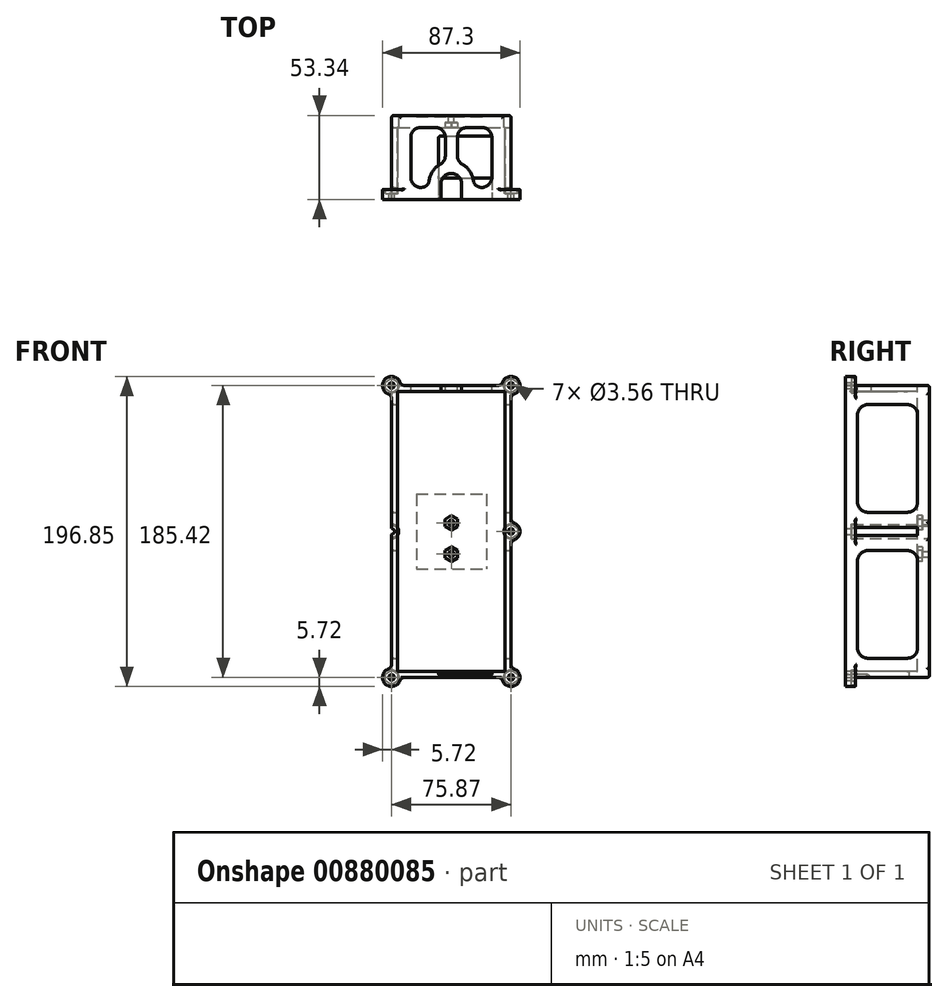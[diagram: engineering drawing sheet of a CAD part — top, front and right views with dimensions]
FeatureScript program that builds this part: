
annotation { "Feature Type Name" : "Feature", "Feature Type Description" : "" }
export const myFeature = defineFeature(function(context is Context, id is Id, definition is map)
    precondition{}
    {
        {
            var Q0;
            Q0=qCreatedBy(makeId("Front.planeOp"),FACE);
            var sketch = newSketch(context, id + "F0", { "sketchPlane" : qUnion([Q0])});
            skLineSegment(sketch, "E0.bottom", {"start": v(0, 0) * mm, "end": v(75.87, 0) * mm});
            skLineSegment(sketch, "E0.top", {"start": v(0, 185.42) * mm, "end": v(75.87, 185.42) * mm});
            skLineSegment(sketch, "E0.left", {"start": v(0, 0) * mm, "end": v(0, 185.42) * mm});
            skLineSegment(sketch, "E0.right", {"start": v(75.87, 0) * mm, "end": v(75.87, 185.42) * mm});
            skSolve(sketch);
        }
        {
            var Q0;
            Q0=makeQuery(id+"F0.imprint","IMPRINT",FACE,{"disambiguationData":[TD([[makeQuery(id+"F0.imprint","IMPRINT",EDGE,{"derivedFrom":sQuery(id+"F0.wireOp",EDGE,"E0.bottom")}),1.0]])]});
            extrude(context, id + "F1", {"entities" : qUnion([Q0]), "oppositeDirection" : true, "depth" : 53.34 * mm, "offsetDistance" : 25.4 * mm});
        }
        {
            var Q0;
            Q0=makeQuery(id+"F1.opExtrude","CAP_FACE",FACE,{"disambiguationData":[OSD([sQuery(id+"F0.wireOp",EDGE,"E0.bottom"),sQuery(id+"F0.wireOp",EDGE,"E0.top"),sQuery(id+"F0.wireOp",EDGE,"E0.left"),sQuery(id+"F0.wireOp",EDGE,"E0.right")])],"isStart":true});
            var sketch = newSketch(context, id + "F2", { "sketchPlane" : qUnion([Q0])});
            skLineSegment(sketch, "E1.0", {"start": v(72.06, 3.8) * mm, "end": v(72.06, 181.6) * mm});
            skLineSegment(sketch, "E2.0", {"start": v(3.81, 3.8) * mm, "end": v(3.8, 181.6) * mm});
            skLineSegment(sketch, "E3.0", {"start": v(3.81, 3.8) * mm, "end": v(72.06, 3.8) * mm});
            skLineSegment(sketch, "E4.0", {"start": v(3.8, 181.6) * mm, "end": v(72.06, 181.6) * mm});
            skSolve(sketch);
        }
        {
            var Q0;
            Q0=makeQuery(id+"F2.imprint","IMPRINT",FACE,{"disambiguationData":[TD([[makeQuery(id+"F2.imprint","IMPRINT",EDGE,{"derivedFrom":sQuery(id+"F2.wireOp",EDGE,"E1.0")}),1.0]])]});
            extrude(context, id + "F3", {"entities" : qUnion([Q0]), "operationType" : NewBodyOperationType.REMOVE, "oppositeDirection" : true, "depth" : 45.72 * mm, "offsetDistance" : 25.4 * mm});
        }
        {
            var Q0;
            Q0=makeQuery(id+"F1.opExtrude","SWEPT_FACE",FACE,{"disambiguationData":[OSD([sQuery(id+"F0.wireOp",EDGE,"E0.top")])]});
            var sketch = newSketch(context, id + "F4", { "sketchPlane" : qUnion([Q0])});
            skLineSegment(sketch, "E5.0", {"start": v(44.48, 0) * mm, "end": v(44.48, 9.98) * mm});
            skLineSegment(sketch, "E6.0", {"start": v(31.4, 0) * mm, "end": v(31.4, 9.98) * mm});
            skLineSegment(sketch, "E7.0", {"start": v(37.92, 16.51) * mm, "end": v(37.95, 16.51) * mm});
            skPoint(sketch, "E8.orphan", {"position": v(37.93, 53.34) * mm});
            skPoint(sketch, "E9.start.orphan", {"position": v(37.93, 0) * mm});
            skPoint(sketch, "E10.visualSharp", {"position": v(31.4, 16.51) * mm});
            skArc(sketch, "E10.filletArc", {"start": v(31.78, 16.51) * mm, "mid": v(31.5, 16.4) * mm, "end": v(31.4, 16.13) * mm});
            skArc(sketch, "E11.filletArc", {"start": v(37.92, 16.51) * mm, "mid": v(33.3, 14.6) * mm, "end": v(31.4, 9.98) * mm});
            skPoint(sketch, "E12.visualSharp", {"position": v(44.48, 16.51) * mm});
            skArc(sketch, "E12.filletArc", {"start": v(44.48, 9.98) * mm, "mid": v(42.56, 14.6) * mm, "end": v(37.95, 16.51) * mm});
            skLineSegment(sketch, "E13", {"start": v(44.48, 0) * mm, "end": v(31.4, 0) * mm});
            skSolve(sketch);
        }
        {
            var Q0;
            Q0=makeQuery(id+"F4.imprint","IMPRINT",FACE,{"disambiguationData":[TD([[makeQuery(id+"F4.imprint","IMPRINT",EDGE,{"derivedFrom":sQuery(id+"F4.wireOp",EDGE,"E5.0")}),1.0]])]});
            extrude(context, id + "F5", {"entities" : qUnion([Q0]), "operationType" : NewBodyOperationType.REMOVE, "oppositeDirection" : true, "depth" : 5.08 * mm, "offsetDistance" : 25.4 * mm});
        }
        {
            var Q0;
            Q0=makeQuery(id+"F1.opExtrude","SWEPT_FACE",FACE,{"disambiguationData":[OSD([sQuery(id+"F0.wireOp",EDGE,"E0.bottom")])]});
            var sketch = newSketch(context, id + "F6", { "sketchPlane" : qUnion([Q0])});
            skPoint(sketch, "E14.0", {"position": v(0, -53.34) * mm});
            skLineSegment(sketch, "E15.0", {"start": v(29.72, -38.86) * mm, "end": v(29.72, -14.73) * mm});
            skLineSegment(sketch, "E16.0", {"start": v(30.99, -40.13) * mm, "end": v(62.66, -40.13) * mm});
            skLineSegment(sketch, "E17.0", {"start": v(63.93, -38.86) * mm, "end": v(63.93, -14.73) * mm});
            skLineSegment(sketch, "E18.0", {"start": v(30.99, -13.46) * mm, "end": v(62.66, -13.46) * mm});
            skPoint(sketch, "E19.visualSharp", {"position": v(29.72, -13.46) * mm});
            skArc(sketch, "E19.filletArc", {"start": v(30.99, -13.46) * mm, "mid": v(30.09, -13.83) * mm, "end": v(29.72, -14.73) * mm});
            skPoint(sketch, "E20.visualSharp", {"position": v(29.72, -40.13) * mm});
            skArc(sketch, "E20.filletArc", {"start": v(29.72, -38.86) * mm, "mid": v(30.09, -39.76) * mm, "end": v(30.99, -40.13) * mm});
            skPoint(sketch, "E21.visualSharp", {"position": v(63.93, -13.46) * mm});
            skArc(sketch, "E21.filletArc", {"start": v(63.93, -14.73) * mm, "mid": v(63.56, -13.83) * mm, "end": v(62.66, -13.46) * mm});
            skPoint(sketch, "E22.visualSharp", {"position": v(63.93, -40.13) * mm});
            skArc(sketch, "E22.filletArc", {"start": v(62.66, -40.13) * mm, "mid": v(63.56, -39.76) * mm, "end": v(63.93, -38.86) * mm});
            skSolve(sketch);
        }
        {
            var Q0;
            Q0=makeQuery(id+"F6.imprint","IMPRINT",FACE,{"disambiguationData":[TD([[makeQuery(id+"F6.imprint","IMPRINT",EDGE,{"derivedFrom":sQuery(id+"F6.wireOp",EDGE,"E15.0")}),-1.0]])]});
            extrude(context, id + "F7", {"entities" : qUnion([Q0]), "operationType" : NewBodyOperationType.REMOVE, "oppositeDirection" : true, "depth" : 5.08 * mm, "offsetDistance" : 25.4 * mm});
        }
        {
            var Q0;
            Q0=makeQuery(id+"F1.opExtrude","CAP_FACE",FACE,{"disambiguationData":[OSD([sQuery(id+"F0.wireOp",EDGE,"E0.bottom"),sQuery(id+"F0.wireOp",EDGE,"E0.top"),sQuery(id+"F0.wireOp",EDGE,"E0.left"),sQuery(id+"F0.wireOp",EDGE,"E0.right")])],"isStart":true});
            var sketch = newSketch(context, id + "F8", { "sketchPlane" : qUnion([Q0])});
            skArc(sketch, "E23", {"start": v(4.57, 182) * mm, "mid": v(-4.04, 189.46) * mm, "end": v(3.43, 180.85) * mm});
            skArc(sketch, "E24", {"start": v(72.44, 180.85) * mm, "mid": v(79.91, 189.46) * mm, "end": v(71.3, 182) * mm});
            skArc(sketch, "E25", {"start": v(3.43, 4.57) * mm, "mid": v(-4.04, -4.04) * mm, "end": v(4.57, 3.43) * mm});
            skArc(sketch, "E26", {"start": v(71.3, 3.43) * mm, "mid": v(79.91, -4.04) * mm, "end": v(72.44, 4.57) * mm});
            skArc(sketch, "E27", {"start": v(72.44, 88.14) * mm, "mid": v(81.58, 92.71) * mm, "end": v(72.44, 97.28) * mm});
            skArc(sketch, "E28", {"start": v(3.43, 97.28) * mm, "mid": v(-5.71, 92.71) * mm, "end": v(3.43, 88.14) * mm});
            skLineSegment(sketch, "E29.0", {"start": v(3.43, 3.43) * mm, "end": v(3.43, 4.57) * mm});
            skLineSegment(sketch, "E30.trimOffspring", {"start": v(3.43, 180.85) * mm, "end": v(3.43, 182) * mm});
            skLineSegment(sketch, "E31.trimOffspring", {"start": v(3.43, 88.14) * mm, "end": v(3.43, 97.28) * mm});
            skLineSegment(sketch, "E32.0", {"start": v(72.44, 3.43) * mm, "end": v(72.44, 4.57) * mm});
            skLineSegment(sketch, "E33.trimOffspring", {"start": v(72.44, 180.85) * mm, "end": v(72.44, 182) * mm});
            skLineSegment(sketch, "E34.trimOffspring", {"start": v(72.44, 88.14) * mm, "end": v(72.44, 97.28) * mm});
            skLineSegment(sketch, "E35.0", {"start": v(71.3, 182) * mm, "end": v(72.44, 182) * mm});
            skLineSegment(sketch, "E36.0", {"start": v(3.43, 182) * mm, "end": v(4.57, 182) * mm});
            skLineSegment(sketch, "E37.0", {"start": v(3.43, 3.43) * mm, "end": v(4.57, 3.43) * mm});
            skLineSegment(sketch, "E38.trimOffspring", {"start": v(71.3, 3.43) * mm, "end": v(72.44, 3.43) * mm});
            skSolve(sketch);
        }
        {
            var Q0;
            {var subQ0=sQuery(id+"F8.wireOp",EDGE,"E24");var subQ1=sQuery(id+"F0.wireOp",EDGE,"E0.right");var subQ2=makeQuery(id+"F1.opExtrude","CAP_EDGE",EDGE,{"disambiguationData":[OSD([subQ1])],"isStart":true});var subQ3=makeQuery(id+"F8.imprint","INTERSECT",VERTEX,{"derivedFrom":[subQ2,subQ0]});Q0=makeQuery(id+"F8.imprint","IMPRINT",FACE,{"disambiguationData":[TD([[makeQuery(id+"F8.imprint","IMPRINT",EDGE,{"disambiguationData":[TD([[subQ3,-1.0]])],"derivedFrom":subQ0}),1.0]])]});}
            var Q1;
            {var subQ0=sQuery(id+"F8.wireOp",EDGE,"E23");var subQ1=sQuery(id+"F0.wireOp",EDGE,"E0.left");var subQ5=makeQuery(id+"F1.opExtrude","CAP_EDGE",EDGE,{"disambiguationData":[OSD([subQ1])],"isStart":true});var subQ6=makeQuery(id+"F8.imprint","INTERSECT",VERTEX,{"derivedFrom":[subQ5,subQ0]});Q1=makeQuery(id+"F8.imprint","IMPRINT",FACE,{"disambiguationData":[TD([[makeQuery(id+"F8.imprint","IMPRINT",EDGE,{"disambiguationData":[TD([[subQ6,1.0]])],"derivedFrom":subQ0}),1.0]])]});}
            var Q2;
            {var subQ0=sQuery(id+"F8.wireOp",EDGE,"E28");var subQ1=makeQuery(id+"F1.opExtrude","CAP_EDGE",EDGE,{"disambiguationData":[OSD([sQuery(id+"F0.wireOp",EDGE,"E0.left")])],"isStart":true});var subQ2=makeQuery(id+"F8.imprint","INTERSECT",VERTEX,{"disambiguationData":[OD(0.0)],"derivedFrom":[subQ1,subQ0]});Q2=makeQuery(id+"F8.imprint","IMPRINT",FACE,{"disambiguationData":[TD([[makeQuery(id+"F8.imprint","IMPRINT",EDGE,{"disambiguationData":[TD([[subQ2,-1.0]])],"derivedFrom":subQ0}),1.0]])]});}
            var Q3;
            {var subQ0=sQuery(id+"F8.wireOp",EDGE,"E31.trimOffspring");Q3=makeQuery(id+"F8.imprint","IMPRINT",FACE,{"disambiguationData":[TD([[makeQuery(id+"F8.imprint","IMPRINT",EDGE,{"derivedFrom":subQ0}),1.0]])]});}
            var Q4;
            {var subQ0=sQuery(id+"F8.wireOp",EDGE,"E27");var subQ1=makeQuery(id+"F1.opExtrude","CAP_EDGE",EDGE,{"disambiguationData":[OSD([sQuery(id+"F0.wireOp",EDGE,"E0.right")])],"isStart":true});var subQ2=makeQuery(id+"F8.imprint","INTERSECT",VERTEX,{"disambiguationData":[OD(0.0)],"derivedFrom":[subQ1,subQ0]});Q4=makeQuery(id+"F8.imprint","IMPRINT",FACE,{"disambiguationData":[TD([[makeQuery(id+"F8.imprint","IMPRINT",EDGE,{"disambiguationData":[TD([[subQ2,-1.0]])],"derivedFrom":subQ0}),1.0]])]});}
            var Q5;
            {var subQ0=sQuery(id+"F8.wireOp",EDGE,"E34.trimOffspring");Q5=makeQuery(id+"F8.imprint","IMPRINT",FACE,{"disambiguationData":[TD([[makeQuery(id+"F8.imprint","IMPRINT",EDGE,{"derivedFrom":subQ0}),-1.0]])]});}
            var Q6;
            {var subQ1=sQuery(id+"F8.wireOp",EDGE,"E33.trimOffspring");Q6=makeQuery(id+"F8.imprint","IMPRINT",FACE,{"disambiguationData":[TD([[makeQuery(id+"F8.imprint","IMPRINT",EDGE,{"derivedFrom":subQ1}),-1.0]])]});}
            var Q7;
            {var subQ0=sQuery(id+"F8.wireOp",EDGE,"E30.trimOffspring");Q7=makeQuery(id+"F8.imprint","IMPRINT",FACE,{"disambiguationData":[TD([[makeQuery(id+"F8.imprint","IMPRINT",EDGE,{"derivedFrom":subQ0}),1.0]])]});}
            var Q8;
            {var subQ0=sQuery(id+"F8.wireOp",EDGE,"E26");var subQ1=makeQuery(id+"F1.opExtrude","CAP_EDGE",EDGE,{"disambiguationData":[OSD([sQuery(id+"F0.wireOp",EDGE,"E0.bottom")])],"isStart":true});var subQ2=makeQuery(id+"F8.imprint","INTERSECT",VERTEX,{"derivedFrom":[subQ1,subQ0]});Q8=makeQuery(id+"F8.imprint","IMPRINT",FACE,{"disambiguationData":[TD([[makeQuery(id+"F8.imprint","IMPRINT",EDGE,{"disambiguationData":[TD([[subQ2,-1.0]])],"derivedFrom":subQ0}),1.0]])]});}
            var Q9;
            {var subQ1=sQuery(id+"F8.wireOp",EDGE,"E32.0");Q9=makeQuery(id+"F8.imprint","IMPRINT",FACE,{"disambiguationData":[TD([[makeQuery(id+"F8.imprint","IMPRINT",EDGE,{"derivedFrom":subQ1}),-1.0]])]});}
            var Q10;
            {var subQ0=sQuery(id+"F8.wireOp",EDGE,"E29.0");Q10=makeQuery(id+"F8.imprint","IMPRINT",FACE,{"disambiguationData":[TD([[makeQuery(id+"F8.imprint","IMPRINT",EDGE,{"derivedFrom":subQ0}),1.0]])]});}
            var Q11;
            {var subQ0=sQuery(id+"F8.wireOp",EDGE,"E25");var subQ1=makeQuery(id+"F1.opExtrude","CAP_EDGE",EDGE,{"disambiguationData":[OSD([sQuery(id+"F0.wireOp",EDGE,"E0.left")])],"isStart":true});var subQ2=makeQuery(id+"F8.imprint","INTERSECT",VERTEX,{"derivedFrom":[subQ1,subQ0]});Q11=makeQuery(id+"F8.imprint","IMPRINT",FACE,{"disambiguationData":[TD([[makeQuery(id+"F8.imprint","IMPRINT",EDGE,{"disambiguationData":[TD([[subQ2,-1.0]])],"derivedFrom":subQ0}),1.0]])]});}
            extrude(context, id + "F9", {"entities" : qUnion([Q0, Q1, Q2, Q3, Q4, Q5, Q6, Q7, Q8, Q9, Q10, Q11]), "operationType" : NewBodyOperationType.ADD, "oppositeDirection" : true, "depth" : 6.35 * mm, "offsetDistance" : 25.4 * mm});
        }
        {
            var Q0;
            Q0=makeQuery(id+"F1.opExtrude","CAP_FACE",FACE,{"disambiguationData":[OSD([sQuery(id+"F0.wireOp",EDGE,"E0.bottom"),sQuery(id+"F0.wireOp",EDGE,"E0.top"),sQuery(id+"F0.wireOp",EDGE,"E0.left"),sQuery(id+"F0.wireOp",EDGE,"E0.right")])],"isStart":false});
            var sketch = newSketch(context, id + "F10", { "sketchPlane" : qUnion([Q0])});
            skCircle(sketch, "E39", {"center": v(-75.87, 185.42) * mm, "radius": 4.57 * mm});
            skCircle(sketch, "E40", {"center": v(0, 185.42) * mm, "radius": 4.57 * mm});
            skCircle(sketch, "E41", {"center": v(0, 92.71) * mm, "radius": 4.57 * mm});
            skCircle(sketch, "E42", {"center": v(-75.87, 92.71) * mm, "radius": 4.57 * mm});
            skCircle(sketch, "E43", {"center": v(0, 0) * mm, "radius": 4.57 * mm});
            skCircle(sketch, "E44", {"center": v(-75.87, 0) * mm, "radius": 4.57 * mm});
            skSolve(sketch);
        }
        {
            var Q0;
            {var subQ0=sQuery(id+"F10.wireOp",EDGE,"E39");var subQ1=makeQuery(id+"F1.opExtrude","CAP_EDGE",EDGE,{"disambiguationData":[OSD([sQuery(id+"F0.wireOp",EDGE,"E0.top")])],"isStart":false});var subQ2=makeQuery(id+"F10.imprint","INTERSECT",VERTEX,{"derivedFrom":[subQ1,subQ0]});Q0=makeQuery(id+"F10.imprint","IMPRINT",FACE,{"disambiguationData":[TD([[makeQuery(id+"F10.imprint","IMPRINT",EDGE,{"disambiguationData":[TD([[subQ2,-1.0]])],"derivedFrom":subQ0}),1.0]])]});}
            var Q1;
            {var subQ0=sQuery(id+"F10.wireOp",EDGE,"E39");var subQ1=makeQuery(id+"F1.opExtrude","CAP_EDGE",EDGE,{"disambiguationData":[OSD([sQuery(id+"F0.wireOp",EDGE,"E0.top")])],"isStart":false});var subQ2=makeQuery(id+"F10.imprint","INTERSECT",VERTEX,{"derivedFrom":[subQ1,subQ0]});Q1=makeQuery(id+"F10.imprint","IMPRINT",FACE,{"disambiguationData":[TD([[makeQuery(id+"F10.imprint","IMPRINT",EDGE,{"disambiguationData":[TD([[subQ2,1.0]])],"derivedFrom":subQ0}),1.0]])]});}
            var Q2;
            {var subQ0=sQuery(id+"F10.wireOp",EDGE,"E42");var subQ1=makeQuery(id+"F1.opExtrude","CAP_EDGE",EDGE,{"disambiguationData":[OSD([sQuery(id+"F0.wireOp",EDGE,"E0.right")])],"isStart":false});var subQ2=makeQuery(id+"F10.imprint","INTERSECT",VERTEX,{"disambiguationData":[OD(0.0)],"derivedFrom":[subQ1,subQ0]});Q2=makeQuery(id+"F10.imprint","IMPRINT",FACE,{"disambiguationData":[TD([[makeQuery(id+"F10.imprint","IMPRINT",EDGE,{"disambiguationData":[TD([[subQ2,-1.0]])],"derivedFrom":subQ0}),1.0]])]});}
            var Q3;
            {var subQ0=sQuery(id+"F10.wireOp",EDGE,"E42");var subQ1=makeQuery(id+"F1.opExtrude","CAP_EDGE",EDGE,{"disambiguationData":[OSD([sQuery(id+"F0.wireOp",EDGE,"E0.right")])],"isStart":false});var subQ2=makeQuery(id+"F10.imprint","INTERSECT",VERTEX,{"disambiguationData":[OD(0.0)],"derivedFrom":[subQ1,subQ0]});Q3=makeQuery(id+"F10.imprint","IMPRINT",FACE,{"disambiguationData":[TD([[makeQuery(id+"F10.imprint","IMPRINT",EDGE,{"disambiguationData":[TD([[subQ2,1.0]])],"derivedFrom":subQ0}),1.0]])]});}
            var Q4;
            {var subQ0=sQuery(id+"F10.wireOp",EDGE,"E41");var subQ1=makeQuery(id+"F1.opExtrude","CAP_EDGE",EDGE,{"disambiguationData":[OSD([sQuery(id+"F0.wireOp",EDGE,"E0.left")])],"isStart":false});var subQ2=makeQuery(id+"F10.imprint","INTERSECT",VERTEX,{"disambiguationData":[OD(0.0)],"derivedFrom":[subQ1,subQ0]});Q4=makeQuery(id+"F10.imprint","IMPRINT",FACE,{"disambiguationData":[TD([[makeQuery(id+"F10.imprint","IMPRINT",EDGE,{"disambiguationData":[TD([[subQ2,1.0]])],"derivedFrom":subQ0}),1.0]])]});}
            var Q5;
            {var subQ0=sQuery(id+"F10.wireOp",EDGE,"E41");var subQ1=makeQuery(id+"F1.opExtrude","CAP_EDGE",EDGE,{"disambiguationData":[OSD([sQuery(id+"F0.wireOp",EDGE,"E0.left")])],"isStart":false});var subQ2=makeQuery(id+"F10.imprint","INTERSECT",VERTEX,{"disambiguationData":[OD(0.0)],"derivedFrom":[subQ1,subQ0]});Q5=makeQuery(id+"F10.imprint","IMPRINT",FACE,{"disambiguationData":[TD([[makeQuery(id+"F10.imprint","IMPRINT",EDGE,{"disambiguationData":[TD([[subQ2,-1.0]])],"derivedFrom":subQ0}),1.0]])]});}
            var Q6;
            {var subQ0=sQuery(id+"F10.wireOp",EDGE,"E40");var subQ1=makeQuery(id+"F1.opExtrude","CAP_EDGE",EDGE,{"disambiguationData":[OSD([sQuery(id+"F0.wireOp",EDGE,"E0.top")])],"isStart":false});var subQ2=makeQuery(id+"F10.imprint","INTERSECT",VERTEX,{"derivedFrom":[subQ1,subQ0]});Q6=makeQuery(id+"F10.imprint","IMPRINT",FACE,{"disambiguationData":[TD([[makeQuery(id+"F10.imprint","IMPRINT",EDGE,{"disambiguationData":[TD([[subQ2,1.0]])],"derivedFrom":subQ0}),1.0]])]});}
            var Q7;
            {var subQ0=sQuery(id+"F10.wireOp",EDGE,"E40");var subQ1=makeQuery(id+"F1.opExtrude","CAP_EDGE",EDGE,{"disambiguationData":[OSD([sQuery(id+"F0.wireOp",EDGE,"E0.top")])],"isStart":false});var subQ2=makeQuery(id+"F10.imprint","INTERSECT",VERTEX,{"derivedFrom":[subQ1,subQ0]});Q7=makeQuery(id+"F10.imprint","IMPRINT",FACE,{"disambiguationData":[TD([[makeQuery(id+"F10.imprint","IMPRINT",EDGE,{"disambiguationData":[TD([[subQ2,-1.0]])],"derivedFrom":subQ0}),1.0]])]});}
            var Q8;
            {var subQ0=sQuery(id+"F10.wireOp",EDGE,"E43");var subQ1=makeQuery(id+"F1.opExtrude","CAP_EDGE",EDGE,{"disambiguationData":[OSD([sQuery(id+"F0.wireOp",EDGE,"E0.bottom")])],"isStart":false});var subQ2=makeQuery(id+"F10.imprint","INTERSECT",VERTEX,{"derivedFrom":[subQ1,subQ0]});Q8=makeQuery(id+"F10.imprint","IMPRINT",FACE,{"disambiguationData":[TD([[makeQuery(id+"F10.imprint","IMPRINT",EDGE,{"disambiguationData":[TD([[subQ2,-1.0]])],"derivedFrom":subQ0}),1.0]])]});}
            var Q9;
            {var subQ0=sQuery(id+"F10.wireOp",EDGE,"E43");var subQ1=makeQuery(id+"F1.opExtrude","CAP_EDGE",EDGE,{"disambiguationData":[OSD([sQuery(id+"F0.wireOp",EDGE,"E0.bottom")])],"isStart":false});var subQ2=makeQuery(id+"F10.imprint","INTERSECT",VERTEX,{"derivedFrom":[subQ1,subQ0]});Q9=makeQuery(id+"F10.imprint","IMPRINT",FACE,{"disambiguationData":[TD([[makeQuery(id+"F10.imprint","IMPRINT",EDGE,{"disambiguationData":[TD([[subQ2,1.0]])],"derivedFrom":subQ0}),1.0]])]});}
            var Q10;
            {var subQ0=sQuery(id+"F10.wireOp",EDGE,"E44");var subQ1=makeQuery(id+"F1.opExtrude","CAP_EDGE",EDGE,{"disambiguationData":[OSD([sQuery(id+"F0.wireOp",EDGE,"E0.bottom")])],"isStart":false});var subQ2=makeQuery(id+"F10.imprint","INTERSECT",VERTEX,{"derivedFrom":[subQ1,subQ0]});Q10=makeQuery(id+"F10.imprint","IMPRINT",FACE,{"disambiguationData":[TD([[makeQuery(id+"F10.imprint","IMPRINT",EDGE,{"disambiguationData":[TD([[subQ2,1.0]])],"derivedFrom":subQ0}),1.0]])]});}
            var Q11;
            {var subQ0=sQuery(id+"F10.wireOp",EDGE,"E44");var subQ1=makeQuery(id+"F1.opExtrude","CAP_EDGE",EDGE,{"disambiguationData":[OSD([sQuery(id+"F0.wireOp",EDGE,"E0.bottom")])],"isStart":false});var subQ2=makeQuery(id+"F10.imprint","INTERSECT",VERTEX,{"derivedFrom":[subQ1,subQ0]});Q11=makeQuery(id+"F10.imprint","IMPRINT",FACE,{"disambiguationData":[TD([[makeQuery(id+"F10.imprint","IMPRINT",EDGE,{"disambiguationData":[TD([[subQ2,-1.0]])],"derivedFrom":subQ0}),1.0]])]});}
            var Q12;
            Q12=makeQuery(id+"F9.opExtrude","CAP_FACE",FACE,{"disambiguationData":[OSD([sQuery(id+"F8.wireOp",EDGE,"E24"),sQuery(id+"F8.wireOp",EDGE,"E33.trimOffspring"),sQuery(id+"F8.wireOp",EDGE,"E35.0")])],"isStart":false});
            extrude(context, id + "F11", {"entities" : qUnion([Q0, Q1, Q2, Q3, Q4, Q5, Q6, Q7, Q8, Q9, Q10, Q11]), "operationType" : NewBodyOperationType.REMOVE, "endBound" : BoundingType.UP_TO_SURFACE, "oppositeDirection" : true, "depth" : 25.4 * mm, "endBoundEntityFace" : qUnion([Q12]), "offsetDistance" : 25.4 * mm});
        }
        {
            var Q0;
            {var subQ5=sQuery(id+"F8.wireOp",EDGE,"E24");var subQ6=sQuery(id+"F0.wireOp",EDGE,"E0.right");Q0=makeQuery(id+"F11.boolean.opBoolean","SPLIT",FACE,{"disambiguationData":[TD([makeQuery(id+"F9.opExtrude","SWEPT_FACE",FACE,{"disambiguationData":[OSD([subQ5])]})])],"derivedFrom":makeQuery(id+"F1.opExtrude","SWEPT_FACE",FACE,{"disambiguationData":[OSD([subQ6])]})});}
            var sketch = newSketch(context, id + "F12", { "sketchPlane" : qUnion([Q0])});
            skLineSegment(sketch, "E45.0", {"start": v(7.62, 111.25) * mm, "end": v(7.62, 166.88) * mm});
            skLineSegment(sketch, "E46.0", {"start": v(45.72, 111.25) * mm, "end": v(45.72, 166.88) * mm});
            skLineSegment(sketch, "E47.0", {"start": v(13.97, 173.23) * mm, "end": v(39.37, 173.23) * mm});
            skLineSegment(sketch, "E48.0", {"start": v(39.37, 104.9) * mm, "end": v(13.97, 104.9) * mm});
            skPoint(sketch, "E49.visualSharp", {"position": v(7.62, 173.23) * mm});
            skArc(sketch, "E49.filletArc", {"start": v(13.97, 173.23) * mm, "mid": v(9.48, 171.37) * mm, "end": v(7.62, 166.88) * mm});
            skPoint(sketch, "E50.visualSharp", {"position": v(45.72, 173.23) * mm});
            skArc(sketch, "E50.filletArc", {"start": v(45.72, 166.88) * mm, "mid": v(43.86, 171.37) * mm, "end": v(39.37, 173.23) * mm});
            skPoint(sketch, "E51.visualSharp", {"position": v(45.72, 104.9) * mm});
            skArc(sketch, "E51.filletArc", {"start": v(39.37, 104.9) * mm, "mid": v(43.86, 106.76) * mm, "end": v(45.72, 111.25) * mm});
            skPoint(sketch, "E52.visualSharp", {"position": v(7.62, 104.9) * mm});
            skArc(sketch, "E52.filletArc", {"start": v(7.62, 111.25) * mm, "mid": v(9.48, 106.76) * mm, "end": v(13.97, 104.9) * mm});
            skLineSegment(sketch, "E53.0", {"start": v(45.72, 18.54) * mm, "end": v(45.72, 74.17) * mm});
            skLineSegment(sketch, "E54.0", {"start": v(7.62, 18.54) * mm, "end": v(7.62, 74.17) * mm});
            skLineSegment(sketch, "E55.0", {"start": v(13.97, 80.52) * mm, "end": v(39.37, 80.52) * mm});
            skLineSegment(sketch, "E56.0", {"start": v(39.37, 12.2) * mm, "end": v(13.97, 12.2) * mm});
            skPoint(sketch, "E57.visualSharp", {"position": v(7.62, 12.2) * mm});
            skArc(sketch, "E57.filletArc", {"start": v(7.62, 18.54) * mm, "mid": v(9.48, 14.05) * mm, "end": v(13.97, 12.2) * mm});
            skPoint(sketch, "E58.visualSharp", {"position": v(45.72, 12.2) * mm});
            skArc(sketch, "E58.filletArc", {"start": v(39.37, 12.2) * mm, "mid": v(43.86, 14.05) * mm, "end": v(45.72, 18.54) * mm});
            skPoint(sketch, "E59.visualSharp", {"position": v(45.72, 80.52) * mm});
            skArc(sketch, "E59.filletArc", {"start": v(45.72, 74.17) * mm, "mid": v(43.86, 78.66) * mm, "end": v(39.37, 80.52) * mm});
            skPoint(sketch, "E60.visualSharp", {"position": v(7.62, 80.52) * mm});
            skArc(sketch, "E60.filletArc", {"start": v(13.97, 80.52) * mm, "mid": v(9.48, 78.66) * mm, "end": v(7.62, 74.17) * mm});
            skSolve(sketch);
        }
        {
            var Q0;
            Q0=makeQuery(id+"F12.imprint","IMPRINT",FACE,{"disambiguationData":[TD([[makeQuery(id+"F12.imprint","IMPRINT",EDGE,{"derivedFrom":sQuery(id+"F12.wireOp",EDGE,"E45.0")}),-1.0]])]});
            var Q1;
            Q1=makeQuery(id+"F12.imprint","IMPRINT",FACE,{"disambiguationData":[TD([[makeQuery(id+"F12.imprint","IMPRINT",EDGE,{"derivedFrom":sQuery(id+"F12.wireOp",EDGE,"E53.0")}),1.0]])]});
            extrude(context, id + "F13", {"entities" : qUnion([Q0, Q1]), "operationType" : NewBodyOperationType.REMOVE, "endBound" : BoundingType.THROUGH_ALL, "oppositeDirection" : true, "depth" : 63.5 * mm, "offsetDistance" : 25.4 * mm});
        }
        {
            var Q0;
            Q0=makeQuery(id+"F1.opExtrude","SWEPT_FACE",FACE,{"disambiguationData":[OSD([sQuery(id+"F0.wireOp",EDGE,"E0.top")])]});
            var sketch = newSketch(context, id + "F14", { "sketchPlane" : qUnion([Q0])});
            skLineSegment(sketch, "E61.0", {"start": v(48.1, 45.72) * mm, "end": v(57.33, 45.72) * mm});
            skArc(sketch, "E62.0", {"start": v(51.95, 11.98) * mm, "mid": v(49.65, 17.94) * mm, "end": v(44.96, 22.27) * mm});
            skArc(sketch, "E63.0", {"start": v(30.93, 22.28) * mm, "mid": v(26.23, 17.94) * mm, "end": v(23.92, 11.98) * mm});
            skLineSegment(sketch, "E64.0", {"start": v(18.54, 7.62) * mm, "end": v(18.89, 7.62) * mm});
            skLineSegment(sketch, "E65.0", {"start": v(12.2, 39.37) * mm, "end": v(12.2, 13.97) * mm});
            skLineSegment(sketch, "E66.0", {"start": v(63.68, 13.97) * mm, "end": v(63.68, 39.37) * mm});
            skLineSegment(sketch, "E67.0", {"start": v(56.98, 7.62) * mm, "end": v(57.33, 7.62) * mm});
            skLineSegment(sketch, "E68.0", {"start": v(41.76, 27.78) * mm, "end": v(41.76, 39.37) * mm});
            skLineSegment(sketch, "E69.0", {"start": v(34.14, 27.8) * mm, "end": v(34.14, 39.37) * mm});
            skArc(sketch, "E70.filletArc", {"start": v(30.93, 22.28) * mm, "mid": v(33.28, 24.6) * mm, "end": v(34.14, 27.8) * mm});
            skArc(sketch, "E71.filletArc", {"start": v(41.76, 27.78) * mm, "mid": v(42.62, 24.6) * mm, "end": v(44.96, 22.27) * mm});
            skArc(sketch, "E72.filletArc", {"start": v(48.1, 45.72) * mm, "mid": v(43.62, 43.86) * mm, "end": v(41.76, 39.37) * mm});
            skLineSegment(sketch, "E73", {"start": v(27.79, 45.72) * mm, "end": v(18.54, 45.72) * mm});
            skPoint(sketch, "E74.visualSharp", {"position": v(34.14, 45.72) * mm});
            skArc(sketch, "E74.filletArc", {"start": v(34.14, 39.37) * mm, "mid": v(32.28, 43.86) * mm, "end": v(27.79, 45.72) * mm});
            skPoint(sketch, "E75.visualSharp", {"position": v(12.2, 45.72) * mm});
            skArc(sketch, "E75.filletArc", {"start": v(18.54, 45.72) * mm, "mid": v(14.05, 43.86) * mm, "end": v(12.2, 39.37) * mm});
            skPoint(sketch, "E76.visualSharp", {"position": v(12.2, 7.62) * mm});
            skArc(sketch, "E76.filletArc", {"start": v(12.2, 13.97) * mm, "mid": v(14.05, 9.48) * mm, "end": v(18.54, 7.62) * mm});
            skPoint(sketch, "E77.visualSharp", {"position": v(63.68, 7.62) * mm});
            skArc(sketch, "E77.filletArc", {"start": v(57.33, 7.62) * mm, "mid": v(61.82, 9.48) * mm, "end": v(63.68, 13.97) * mm});
            skArc(sketch, "E78.filletArc", {"start": v(18.89, 7.62) * mm, "mid": v(22.22, 8.86) * mm, "end": v(23.92, 11.98) * mm});
            skArc(sketch, "E79.filletArc", {"start": v(51.95, 11.98) * mm, "mid": v(53.65, 8.86) * mm, "end": v(56.98, 7.62) * mm});
            skPoint(sketch, "E80.visualSharp", {"position": v(63.68, 45.72) * mm});
            skArc(sketch, "E80.filletArc", {"start": v(63.68, 39.37) * mm, "mid": v(61.82, 43.86) * mm, "end": v(57.33, 45.72) * mm});
            skSolve(sketch);
        }
        {
            var Q0;
            Q0=makeQuery(id+"F14.imprint","IMPRINT",FACE,{"disambiguationData":[TD([[makeQuery(id+"F14.imprint","IMPRINT",EDGE,{"derivedFrom":sQuery(id+"F14.wireOp",EDGE,"E63.0")}),-1.0]])]});
            var Q1;
            Q1=makeQuery(id+"F14.imprint","IMPRINT",FACE,{"disambiguationData":[TD([[makeQuery(id+"F14.imprint","IMPRINT",EDGE,{"derivedFrom":sQuery(id+"F14.wireOp",EDGE,"E61.0")}),-1.0]])]});
            extrude(context, id + "F15", {"entities" : qUnion([Q0, Q1]), "operationType" : NewBodyOperationType.REMOVE, "oppositeDirection" : true, "depth" : 6.35 * mm, "offsetDistance" : 25.4 * mm});
        }
        {
            var Q0;
            Q0=makeQuery(id+"F1.opExtrude","CAP_FACE",FACE,{"disambiguationData":[OSD([sQuery(id+"F0.wireOp",EDGE,"E0.bottom"),sQuery(id+"F0.wireOp",EDGE,"E0.top"),sQuery(id+"F0.wireOp",EDGE,"E0.left"),sQuery(id+"F0.wireOp",EDGE,"E0.right")])],"isStart":false});
            var sketch = newSketch(context, id + "F16", { "sketchPlane" : qUnion([Q0])});
            skLineSegment(sketch, "E81.0", {"start": v(-15.7, 68.9) * mm, "end": v(-60.16, 68.9) * mm});
            skLineSegment(sketch, "E82.0", {"start": v(-15.7, 116.52) * mm, "end": v(-60.16, 116.52) * mm});
            skLineSegment(sketch, "E83.0", {"start": v(-60.16, 116.52) * mm, "end": v(-60.16, 68.9) * mm});
            skLineSegment(sketch, "E84.0", {"start": v(-15.7, 116.52) * mm, "end": v(-15.7, 68.9) * mm});
            skPoint(sketch, "E85.orphan", {"position": v(-75.87, 116.52) * mm});
            skPoint(sketch, "E86.orphan", {"position": v(-75.87, 68.9) * mm});
            skPoint(sketch, "E87.orphan", {"position": v(0, 68.9) * mm});
            skPoint(sketch, "E88.orphan", {"position": v(0, 116.52) * mm});
            skPoint(sketch, "E89.orphan", {"position": v(0, 92.71) * mm});
            skPoint(sketch, "E90.orphan", {"position": v(-75.87, 92.71) * mm});
            skPoint(sketch, "E91.end.orphan", {"position": v(-37.93, 68.9) * mm});
            skPoint(sketch, "E91.start.orphan", {"position": v(-37.93, 116.52) * mm});
            skSolve(sketch);
        }
        {
            var Q0;
            Q0=makeQuery(id+"F16.imprint","IMPRINT",FACE,{"disambiguationData":[TD([[makeQuery(id+"F16.imprint","IMPRINT",EDGE,{"derivedFrom":sQuery(id+"F16.wireOp",EDGE,"E81.0")}),-1.0]])]});
            extrude(context, id + "F17", {"entities" : qUnion([Q0]), "operationType" : NewBodyOperationType.REMOVE, "oppositeDirection" : true, "depth" : 0.76 * mm, "offsetDistance" : 25.4 * mm});
        }
        {
            var Q0;
            Q0=makeQuery(id+"F17.boolean.opBoolean","COPY",FACE,{"derivedFrom":makeQuery(id+"F17.opExtrude","CAP_FACE",FACE,{"disambiguationData":[OSD([sQuery(id+"F16.wireOp",EDGE,"E81.0"),sQuery(id+"F16.wireOp",EDGE,"E82.0"),sQuery(id+"F16.wireOp",EDGE,"E83.0"),sQuery(id+"F16.wireOp",EDGE,"E84.0")])],"isStart":false})});
            var sketch = newSketch(context, id + "F18", { "sketchPlane" : qUnion([Q0])});
            skPoint(sketch, "E92.end.orphan", {"position": v(-60.16, 92.71) * mm});
            skPoint(sketch, "E92.start.orphan", {"position": v(-15.7, 92.71) * mm});
            skCircle(sketch, "E93", {"center": v(-37.93, 98.12) * mm, "radius": 1.78 * mm});
            skCircle(sketch, "E94", {"center": v(-37.93, 78.28) * mm, "radius": 1.78 * mm});
            skPoint(sketch, "E95.orphan", {"position": v(-60.16, 98.12) * mm});
            skPoint(sketch, "E96.0.start.orphan", {"position": v(-15.7, 98.12) * mm});
            skPoint(sketch, "E97.trimOffspring.end.orphan", {"position": v(-60.16, 78.28) * mm});
            skPoint(sketch, "E98.0.start.orphan", {"position": v(-15.7, 78.28) * mm});
            skSolve(sketch);
        }
        {
            var Q0;
            Q0=makeQuery(id+"F18.imprint","IMPRINT",FACE,{"disambiguationData":[TD([[makeQuery(id+"F18.imprint","IMPRINT",EDGE,{"derivedFrom":sQuery(id+"F18.wireOp",EDGE,"E93")}),1.0]])]});
            var Q1;
            Q1=makeQuery(id+"F18.imprint","IMPRINT",FACE,{"disambiguationData":[TD([[makeQuery(id+"F18.imprint","IMPRINT",EDGE,{"derivedFrom":sQuery(id+"F18.wireOp",EDGE,"E94")}),1.0]])]});
            extrude(context, id + "F19", {"entities" : qUnion([Q0, Q1]), "operationType" : NewBodyOperationType.REMOVE, "oppositeDirection" : true, "depth" : 6.35 * mm, "offsetDistance" : 25.4 * mm});
        }
        {
            var Q0;
            Q0=makeQuery(id+"F3.boolean.opBoolean","COPY",FACE,{"derivedFrom":makeQuery(id+"F3.opExtrude","CAP_FACE",FACE,{"disambiguationData":[OSD([sQuery(id+"F2.wireOp",EDGE,"E1.0"),sQuery(id+"F2.wireOp",EDGE,"E2.0"),sQuery(id+"F2.wireOp",EDGE,"E3.0"),sQuery(id+"F2.wireOp",EDGE,"E4.0")])],"isStart":false})});
            var sketch = newSketch(context, id + "F20", { "sketchPlane" : qUnion([Q0])});
            skCircle(sketch, "E99.cCircle", {"center": v(37.93, 98.12) * mm, "radius": 4 * mm, "construction": true});
            skLineSegment(sketch, "E99.0", {"start": v(41.97, 95.87) * mm, "end": v(38, 93.5) * mm});
            skLineSegment(sketch, "E99.1", {"start": v(38, 93.5) * mm, "end": v(33.97, 95.75) * mm});
            skLineSegment(sketch, "E99.2", {"start": v(33.97, 95.75) * mm, "end": v(33.9, 100.37) * mm});
            skLineSegment(sketch, "E99.3", {"start": v(33.9, 100.37) * mm, "end": v(37.86, 102.74) * mm});
            skLineSegment(sketch, "E99.4", {"start": v(37.86, 102.74) * mm, "end": v(41.9, 100.5) * mm});
            skLineSegment(sketch, "E99.5", {"start": v(41.9, 100.5) * mm, "end": v(41.97, 95.87) * mm});
            skPoint(sketch, "E99.0.midPoint", {"position": v(39.99, 94.69) * mm});
            skCircle(sketch, "E100.cCircle", {"center": v(37.93, 78.28) * mm, "radius": 4 * mm, "construction": true});
            skLineSegment(sketch, "E100.0", {"start": v(41.94, 80.6) * mm, "end": v(41.94, 75.97) * mm});
            skLineSegment(sketch, "E100.1", {"start": v(41.94, 75.97) * mm, "end": v(37.93, 73.66) * mm});
            skLineSegment(sketch, "E100.2", {"start": v(37.93, 73.66) * mm, "end": v(33.93, 75.97) * mm});
            skLineSegment(sketch, "E100.3", {"start": v(33.93, 75.97) * mm, "end": v(33.93, 80.6) * mm});
            skLineSegment(sketch, "E100.4", {"start": v(33.93, 80.6) * mm, "end": v(37.93, 82.9) * mm});
            skLineSegment(sketch, "E100.5", {"start": v(37.93, 82.9) * mm, "end": v(41.94, 80.6) * mm});
            skPoint(sketch, "E100.0.midPoint", {"position": v(41.94, 78.28) * mm});
            skSolve(sketch);
        }
        {
            var Q0;
            Q0=makeQuery(id+"F20.imprint","IMPRINT",FACE,{"disambiguationData":[TD([[makeQuery(id+"F20.imprint","IMPRINT",EDGE,{"derivedFrom":sQuery(id+"F20.wireOp",EDGE,"E99.0")}),-1.0]])]});
            var Q1;
            Q1=makeQuery(id+"F20.imprint","IMPRINT",FACE,{"disambiguationData":[TD([[makeQuery(id+"F20.imprint","IMPRINT",EDGE,{"derivedFrom":sQuery(id+"F20.wireOp",EDGE,"E100.0")}),-1.0]])]});
            extrude(context, id + "F21", {"entities" : qUnion([Q0, Q1]), "operationType" : NewBodyOperationType.REMOVE, "oppositeDirection" : true, "depth" : 3.17 * mm, "offsetDistance" : 25.4 * mm});
        }
        {
            var Q0;
            Q0=makeQuery(id+"F1.opExtrude","CAP_FACE",FACE,{"disambiguationData":[OSD([sQuery(id+"F0.wireOp",EDGE,"E0.bottom"),sQuery(id+"F0.wireOp",EDGE,"E0.top"),sQuery(id+"F0.wireOp",EDGE,"E0.left"),sQuery(id+"F0.wireOp",EDGE,"E0.right")])],"isStart":false});
            var sketch = newSketch(context, id + "F22", { "sketchPlane" : qUnion([Q0])});
            skCircle(sketch, "E101", {"center": v(-75.87, 185.42) * mm, "radius": 1.78 * mm});
            skCircle(sketch, "E102", {"center": v(0, 185.42) * mm, "radius": 1.78 * mm});
            skCircle(sketch, "E103", {"center": v(0, 92.71) * mm, "radius": 1.78 * mm});
            skCircle(sketch, "E104", {"center": v(-75.87, 92.71) * mm, "radius": 1.78 * mm});
            skCircle(sketch, "E105", {"center": v(-75.87, 0) * mm, "radius": 1.78 * mm});
            skCircle(sketch, "E106", {"center": v(0, 0) * mm, "radius": 1.78 * mm});
            skSolve(sketch);
        }
        {
            var Q0;
            Q0=makeQuery(id+"F22.imprint","IMPRINT",FACE,{"disambiguationData":[TD([[makeQuery(id+"F22.imprint","IMPRINT",EDGE,{"derivedFrom":sQuery(id+"F22.wireOp",EDGE,"E101")}),1.0]])]});
            var Q1;
            Q1=makeQuery(id+"F22.imprint","IMPRINT",FACE,{"disambiguationData":[TD([[makeQuery(id+"F22.imprint","IMPRINT",EDGE,{"derivedFrom":sQuery(id+"F22.wireOp",EDGE,"E102")}),1.0]])]});
            var Q2;
            Q2=makeQuery(id+"F22.imprint","IMPRINT",FACE,{"disambiguationData":[TD([[makeQuery(id+"F22.imprint","IMPRINT",EDGE,{"derivedFrom":sQuery(id+"F22.wireOp",EDGE,"E103")}),1.0]])]});
            var Q3;
            Q3=makeQuery(id+"F22.imprint","IMPRINT",FACE,{"disambiguationData":[TD([[makeQuery(id+"F22.imprint","IMPRINT",EDGE,{"derivedFrom":sQuery(id+"F22.wireOp",EDGE,"E104")}),1.0]])]});
            var Q4;
            Q4=makeQuery(id+"F22.imprint","IMPRINT",FACE,{"disambiguationData":[TD([[makeQuery(id+"F22.imprint","IMPRINT",EDGE,{"derivedFrom":sQuery(id+"F22.wireOp",EDGE,"E105")}),1.0]])]});
            var Q5;
            Q5=makeQuery(id+"F22.imprint","IMPRINT",FACE,{"disambiguationData":[TD([[makeQuery(id+"F22.imprint","IMPRINT",EDGE,{"derivedFrom":sQuery(id+"F22.wireOp",EDGE,"E106")}),1.0]])]});
            extrude(context, id + "F23", {"entities" : qUnion([Q0, Q1, Q2, Q3, Q4, Q5]), "operationType" : NewBodyOperationType.REMOVE, "endBound" : BoundingType.THROUGH_ALL, "oppositeDirection" : true, "depth" : 25.4 * mm, "offsetDistance" : 25.4 * mm});
        }
        {
            var Q0;
            Q0=makeQuery(id+"F1.opExtrude","CAP_FACE",FACE,{"disambiguationData":[OSD([sQuery(id+"F0.wireOp",EDGE,"E0.bottom"),sQuery(id+"F0.wireOp",EDGE,"E0.top"),sQuery(id+"F0.wireOp",EDGE,"E0.left"),sQuery(id+"F0.wireOp",EDGE,"E0.right")])],"isStart":false});
            var sketch = newSketch(context, id + "F24", { "sketchPlane" : qUnion([Q0])});
            skCircle(sketch, "E107.cCircle", {"center": v(-75.87, 185.42) * mm, "radius": 4 * mm, "construction": true});
            skLineSegment(sketch, "E107.0", {"start": v(-71.87, 187.73) * mm, "end": v(-71.87, 183.11) * mm});
            skLineSegment(sketch, "E107.1", {"start": v(-71.87, 183.11) * mm, "end": v(-75.87, 180.8) * mm});
            skLineSegment(sketch, "E107.2", {"start": v(-75.87, 180.8) * mm, "end": v(-79.87, 183.11) * mm});
            skLineSegment(sketch, "E107.3", {"start": v(-79.87, 183.11) * mm, "end": v(-79.87, 187.73) * mm});
            skLineSegment(sketch, "E107.4", {"start": v(-79.87, 187.73) * mm, "end": v(-75.87, 190.04) * mm});
            skLineSegment(sketch, "E107.5", {"start": v(-75.87, 190.04) * mm, "end": v(-71.87, 187.73) * mm});
            skPoint(sketch, "E107.0.midPoint", {"position": v(-71.87, 185.42) * mm});
            skCircle(sketch, "E108.cCircle", {"center": v(0, 185.42) * mm, "radius": 4 * mm, "construction": true});
            skLineSegment(sketch, "E108.0", {"start": v(-4, 183.11) * mm, "end": v(-4, 187.73) * mm});
            skLineSegment(sketch, "E108.1", {"start": v(-4, 187.73) * mm, "end": v(0, 190.04) * mm});
            skLineSegment(sketch, "E108.2", {"start": v(0, 190.04) * mm, "end": v(4, 187.73) * mm});
            skLineSegment(sketch, "E108.3", {"start": v(4, 187.73) * mm, "end": v(4, 183.11) * mm});
            skLineSegment(sketch, "E108.4", {"start": v(4, 183.11) * mm, "end": v(0, 180.8) * mm});
            skLineSegment(sketch, "E108.5", {"start": v(0, 180.8) * mm, "end": v(-4, 183.11) * mm});
            skPoint(sketch, "E108.0.midPoint", {"position": v(-4, 185.42) * mm});
            skCircle(sketch, "E109.cCircle", {"center": v(0, 92.71) * mm, "radius": 4 * mm, "construction": true});
            skLineSegment(sketch, "E109.0", {"start": v(4, 95.02) * mm, "end": v(4, 90.4) * mm});
            skLineSegment(sketch, "E109.1", {"start": v(4, 90.4) * mm, "end": v(0, 88.1) * mm});
            skLineSegment(sketch, "E109.2", {"start": v(0, 88.1) * mm, "end": v(-4, 90.4) * mm});
            skLineSegment(sketch, "E109.3", {"start": v(-4, 90.4) * mm, "end": v(-4, 95.02) * mm});
            skLineSegment(sketch, "E109.4", {"start": v(-4, 95.02) * mm, "end": v(0, 97.33) * mm});
            skLineSegment(sketch, "E109.5", {"start": v(0, 97.33) * mm, "end": v(4, 95.02) * mm});
            skPoint(sketch, "E109.0.midPoint", {"position": v(4, 92.71) * mm});
            skCircle(sketch, "E110.cCircle", {"center": v(-75.87, 92.71) * mm, "radius": 4 * mm, "construction": true});
            skLineSegment(sketch, "E110.0", {"start": v(-79.87, 90.4) * mm, "end": v(-79.87, 95.02) * mm});
            skLineSegment(sketch, "E110.1", {"start": v(-79.87, 95.02) * mm, "end": v(-75.87, 97.33) * mm});
            skLineSegment(sketch, "E110.2", {"start": v(-75.87, 97.33) * mm, "end": v(-71.87, 95.02) * mm});
            skLineSegment(sketch, "E110.3", {"start": v(-71.87, 95.02) * mm, "end": v(-71.87, 90.4) * mm});
            skLineSegment(sketch, "E110.4", {"start": v(-71.87, 90.4) * mm, "end": v(-75.87, 88.1) * mm});
            skLineSegment(sketch, "E110.5", {"start": v(-75.87, 88.1) * mm, "end": v(-79.87, 90.4) * mm});
            skPoint(sketch, "E110.0.midPoint", {"position": v(-79.87, 92.71) * mm});
            skCircle(sketch, "E111.cCircle", {"center": v(0, 0) * mm, "radius": 4 * mm, "construction": true});
            skLineSegment(sketch, "E111.0", {"start": v(4, 2.3) * mm, "end": v(4, -2.3) * mm});
            skLineSegment(sketch, "E111.1", {"start": v(4, -2.3) * mm, "end": v(0, -4.62) * mm});
            skLineSegment(sketch, "E111.2", {"start": v(0, -4.62) * mm, "end": v(-4, -2.3) * mm});
            skLineSegment(sketch, "E111.3", {"start": v(-4, -2.3) * mm, "end": v(-4, 2.3) * mm});
            skLineSegment(sketch, "E111.4", {"start": v(-4, 2.3) * mm, "end": v(0, 4.62) * mm});
            skLineSegment(sketch, "E111.5", {"start": v(0, 4.62) * mm, "end": v(4, 2.3) * mm});
            skPoint(sketch, "E111.0.midPoint", {"position": v(4, 0) * mm});
            skCircle(sketch, "E112.cCircle", {"center": v(-75.87, 0) * mm, "radius": 4 * mm, "construction": true});
            skLineSegment(sketch, "E112.0", {"start": v(-79.87, -2.3) * mm, "end": v(-79.87, 2.3) * mm});
            skLineSegment(sketch, "E112.1", {"start": v(-79.87, 2.3) * mm, "end": v(-75.87, 4.62) * mm});
            skLineSegment(sketch, "E112.2", {"start": v(-75.87, 4.62) * mm, "end": v(-71.87, 2.3) * mm});
            skLineSegment(sketch, "E112.3", {"start": v(-71.87, 2.3) * mm, "end": v(-71.87, -2.3) * mm});
            skLineSegment(sketch, "E112.4", {"start": v(-71.87, -2.3) * mm, "end": v(-75.87, -4.62) * mm});
            skLineSegment(sketch, "E112.5", {"start": v(-75.87, -4.62) * mm, "end": v(-79.87, -2.3) * mm});
            skPoint(sketch, "E112.0.midPoint", {"position": v(-79.87, 0) * mm});
            skSolve(sketch);
        }
        {
            var Q0;
            {var subQ5=sQuery(id+"F24.wireOp",EDGE,"E107.2");Q0=makeQuery(id+"F24.imprint","IMPRINT",FACE,{"disambiguationData":[TD([[makeQuery(id+"F24.imprint","IMPRINT",EDGE,{"derivedFrom":subQ5}),-1.0]])]});}
            var Q1;
            {var subQ7=sQuery(id+"F24.wireOp",EDGE,"E108.1");Q1=makeQuery(id+"F24.imprint","IMPRINT",FACE,{"disambiguationData":[TD([[makeQuery(id+"F24.imprint","IMPRINT",EDGE,{"derivedFrom":subQ7}),-1.0]])]});}
            var Q2;
            Q2=makeQuery(id+"F24.imprint","IMPRINT",FACE,{"disambiguationData":[TD([[makeQuery(id+"F24.imprint","IMPRINT",EDGE,{"derivedFrom":sQuery(id+"F24.wireOp",EDGE,"E110.0")}),-1.0]])]});
            var Q3;
            Q3=makeQuery(id+"F24.imprint","IMPRINT",FACE,{"disambiguationData":[TD([[makeQuery(id+"F24.imprint","IMPRINT",EDGE,{"derivedFrom":sQuery(id+"F24.wireOp",EDGE,"E109.0")}),-1.0]])]});
            var Q4;
            Q4=makeQuery(id+"F24.imprint","IMPRINT",FACE,{"disambiguationData":[TD([[makeQuery(id+"F24.imprint","IMPRINT",EDGE,{"derivedFrom":sQuery(id+"F24.wireOp",EDGE,"E111.0")}),-1.0]])]});
            var Q5;
            Q5=makeQuery(id+"F24.imprint","IMPRINT",FACE,{"disambiguationData":[TD([[makeQuery(id+"F24.imprint","IMPRINT",EDGE,{"derivedFrom":sQuery(id+"F24.wireOp",EDGE,"E112.0")}),-1.0]])]});
            extrude(context, id + "F25", {"entities" : qUnion([Q0, Q1, Q2, Q3, Q4, Q5]), "operationType" : NewBodyOperationType.REMOVE, "oppositeDirection" : true, "depth" : 49.53 * mm, "offsetDistance" : 25.4 * mm});
        }
        {
            var Q0;
            {var subQ0=sQuery(id+"F0.wireOp",EDGE,"E0.right");Q0=makeQuery(id+"F11.boolean.opBoolean","SPLIT",EDGE,{"disambiguationData":[TD([makeQuery(id+"F11.opExtrude","SWEPT_FACE",FACE,{"disambiguationData":[OSD([sQuery(id+"F10.wireOp",EDGE,"E39")])]})])],"derivedFrom":makeQuery(id+"F1.opExtrude","CAP_EDGE",EDGE,{"disambiguationData":[OSD([subQ0])],"isStart":false})});}
            var Q1;
            Q1=makeQuery(id+"F11.boolean.opBoolean","COPY",EDGE,{"derivedFrom":makeQuery(id+"F11.opExtrude","CAP_EDGE",EDGE,{"disambiguationData":[OSD([sQuery(id+"F10.wireOp",EDGE,"E42")])],"isStart":true})});
            var Q2;
            {var subQ0=sQuery(id+"F0.wireOp",EDGE,"E0.right");Q2=makeQuery(id+"F11.boolean.opBoolean","SPLIT",EDGE,{"disambiguationData":[TD([makeQuery(id+"F11.opExtrude","SWEPT_FACE",FACE,{"disambiguationData":[OSD([sQuery(id+"F10.wireOp",EDGE,"E44")])]})])],"derivedFrom":makeQuery(id+"F1.opExtrude","CAP_EDGE",EDGE,{"disambiguationData":[OSD([subQ0])],"isStart":false})});}
            var Q3;
            Q3=makeQuery(id+"F11.boolean.opBoolean","COPY",EDGE,{"derivedFrom":makeQuery(id+"F11.opExtrude","CAP_EDGE",EDGE,{"disambiguationData":[OSD([sQuery(id+"F10.wireOp",EDGE,"E44")])],"isStart":true})});
            var Q4;
            Q4=makeQuery(id+"F1.opExtrude","CAP_EDGE",EDGE,{"disambiguationData":[OSD([sQuery(id+"F0.wireOp",EDGE,"E0.bottom")])],"isStart":false});
            var Q5;
            Q5=makeQuery(id+"F11.boolean.opBoolean","COPY",EDGE,{"derivedFrom":makeQuery(id+"F11.opExtrude","CAP_EDGE",EDGE,{"disambiguationData":[OSD([sQuery(id+"F10.wireOp",EDGE,"E43")])],"isStart":true})});
            var Q6;
            {var subQ0=sQuery(id+"F0.wireOp",EDGE,"E0.left");Q6=makeQuery(id+"F11.boolean.opBoolean","SPLIT",EDGE,{"disambiguationData":[TD([makeQuery(id+"F11.opExtrude","SWEPT_FACE",FACE,{"disambiguationData":[OSD([sQuery(id+"F10.wireOp",EDGE,"E43")])]})])],"derivedFrom":makeQuery(id+"F1.opExtrude","CAP_EDGE",EDGE,{"disambiguationData":[OSD([subQ0])],"isStart":false})});}
            var Q7;
            Q7=makeQuery(id+"F11.boolean.opBoolean","COPY",EDGE,{"derivedFrom":makeQuery(id+"F11.opExtrude","CAP_EDGE",EDGE,{"disambiguationData":[OSD([sQuery(id+"F10.wireOp",EDGE,"E41")])],"isStart":true})});
            var Q8;
            {var subQ0=sQuery(id+"F0.wireOp",EDGE,"E0.left");Q8=makeQuery(id+"F11.boolean.opBoolean","SPLIT",EDGE,{"disambiguationData":[TD([makeQuery(id+"F11.opExtrude","SWEPT_FACE",FACE,{"disambiguationData":[OSD([sQuery(id+"F10.wireOp",EDGE,"E40")])]})])],"derivedFrom":makeQuery(id+"F1.opExtrude","CAP_EDGE",EDGE,{"disambiguationData":[OSD([subQ0])],"isStart":false})});}
            var Q9;
            Q9=makeQuery(id+"F11.boolean.opBoolean","COPY",EDGE,{"derivedFrom":makeQuery(id+"F11.opExtrude","CAP_EDGE",EDGE,{"disambiguationData":[OSD([sQuery(id+"F10.wireOp",EDGE,"E40")])],"isStart":true})});
            var Q10;
            Q10=makeQuery(id+"F1.opExtrude","CAP_EDGE",EDGE,{"disambiguationData":[OSD([sQuery(id+"F0.wireOp",EDGE,"E0.top")])],"isStart":false});
            var Q11;
            Q11=makeQuery(id+"F11.boolean.opBoolean","COPY",EDGE,{"derivedFrom":makeQuery(id+"F11.opExtrude","CAP_EDGE",EDGE,{"disambiguationData":[OSD([sQuery(id+"F10.wireOp",EDGE,"E39")])],"isStart":true})});
            var Q12;
            Q12=makeQuery(id+"F15.boolean.opBoolean","COPY",EDGE,{"derivedFrom":makeQuery(id+"F15.opExtrude","CAP_EDGE",EDGE,{"disambiguationData":[OSD([sQuery(id+"F14.wireOp",EDGE,"E77.filletArc")])],"isStart":true})});
            var Q13;
            Q13=makeQuery(id+"F15.boolean.opBoolean","COPY",EDGE,{"derivedFrom":makeQuery(id+"F15.opExtrude","CAP_EDGE",EDGE,{"disambiguationData":[OSD([sQuery(id+"F14.wireOp",EDGE,"E70.filletArc")])],"isStart":true})});
            var Q14;
            Q14=makeQuery(id+"F5.boolean.opBoolean","COPY",EDGE,{"derivedFrom":makeQuery(id+"F5.opExtrude","CAP_EDGE",EDGE,{"disambiguationData":[OSD([sQuery(id+"F4.wireOp",EDGE,"E12.filletArc")])],"isStart":true})});
            var Q15;
            Q15=makeQuery(id+"F11.boolean.opBoolean","INTERSECT",EDGE,{"derivedFrom":[makeQuery(id+"F1.opExtrude","SWEPT_FACE",FACE,{"disambiguationData":[OSD([sQuery(id+"F0.wireOp",EDGE,"E0.top")])]}),makeQuery(id+"F11.opExtrude","SWEPT_FACE",FACE,{"disambiguationData":[OSD([sQuery(id+"F10.wireOp",EDGE,"E40")])]})]});
            var Q16;
            {var subQ0=sQuery(id+"F10.wireOp",EDGE,"E40");var subQ1=sQuery(id+"F0.wireOp",EDGE,"E0.left");Q16=makeQuery(id+"F25.boolean.opBoolean","MERGE",EDGE,{"derivedFrom":[makeQuery(id+"F11.boolean.opBoolean","INTERSECT",EDGE,{"derivedFrom":[makeQuery(id+"F1.opExtrude","SWEPT_FACE",FACE,{"disambiguationData":[OSD([subQ1])]}),makeQuery(id+"F11.opExtrude","SWEPT_FACE",FACE,{"disambiguationData":[OSD([subQ0])]})]})],"fromTools":[makeQuery(id+"F25.opExtrude","SWEPT_EDGE",EDGE,{"disambiguationData":[OSD([subQ1,subQ0])]})]});}
            var Q17;
            {var subQ2=sQuery(id+"F0.wireOp",EDGE,"E0.left");var subQ7=sQuery(id+"F8.wireOp",EDGE,"E23");Q17=makeQuery(id+"F13.boolean.opBoolean","INTERSECT",EDGE,{"derivedFrom":[makeQuery(id+"F11.boolean.opBoolean","SPLIT",FACE,{"disambiguationData":[TD([makeQuery(id+"F9.opExtrude","SWEPT_FACE",FACE,{"disambiguationData":[OSD([subQ7])]})])],"derivedFrom":makeQuery(id+"F1.opExtrude","SWEPT_FACE",FACE,{"disambiguationData":[OSD([subQ2])]})}),makeQuery(id+"F13.opExtrude","SWEPT_FACE",FACE,{"disambiguationData":[OSD([sQuery(id+"F12.wireOp",EDGE,"E49.filletArc")])]})]});}
            var Q18;
            {var subQ0=sQuery(id+"F0.wireOp",EDGE,"E0.left");var subQ1=makeQuery(id+"F1.opExtrude","SWEPT_FACE",FACE,{"disambiguationData":[OSD([subQ0])]});var subQ2=sQuery(id+"F10.wireOp",EDGE,"E41");var subQ3=makeQuery(id+"F11.opExtrude","SWEPT_FACE",FACE,{"disambiguationData":[OSD([subQ2])]});Q18=makeQuery(id+"F25.boolean.opBoolean","MERGE",EDGE,{"derivedFrom":[makeQuery(id+"F11.boolean.opBoolean","INTERSECT",EDGE,{"disambiguationData":[OD(0.0)],"derivedFrom":[subQ1,subQ3]})],"fromTools":[makeQuery(id+"F25.opExtrude","SWEPT_EDGE",EDGE,{"disambiguationData":[OSD([subQ0,subQ2]),TDD([makeQuery(id+"F24.imprint","INTERSECT",VERTEX,{"derivedFrom":[makeQuery(id+"F11.boolean.opBoolean","COPY",EDGE,{"derivedFrom":makeQuery(id+"F11.opExtrude","CAP_EDGE",EDGE,{"disambiguationData":[OSD([subQ2])],"isStart":true})}),makeQuery(id+"F11.boolean.opBoolean","SPLIT",EDGE,{"disambiguationData":[TD([makeQuery(id+"F11.opExtrude","SWEPT_FACE",FACE,{"disambiguationData":[OSD([sQuery(id+"F10.wireOp",EDGE,"E40")])]})])],"derivedFrom":makeQuery(id+"F1.opExtrude","CAP_EDGE",EDGE,{"disambiguationData":[OSD([subQ0])],"isStart":false})})]})])]})]});}
            var Q19;
            {var subQ0=sQuery(id+"F0.wireOp",EDGE,"E0.left");var subQ1=makeQuery(id+"F1.opExtrude","SWEPT_FACE",FACE,{"disambiguationData":[OSD([subQ0])]});var subQ2=sQuery(id+"F10.wireOp",EDGE,"E41");var subQ3=makeQuery(id+"F11.opExtrude","SWEPT_FACE",FACE,{"disambiguationData":[OSD([subQ2])]});Q19=makeQuery(id+"F25.boolean.opBoolean","MERGE",EDGE,{"derivedFrom":[makeQuery(id+"F11.boolean.opBoolean","INTERSECT",EDGE,{"disambiguationData":[OD(1.0)],"derivedFrom":[subQ1,subQ3]})],"fromTools":[makeQuery(id+"F25.opExtrude","SWEPT_EDGE",EDGE,{"disambiguationData":[OSD([subQ0,subQ2]),TDD([makeQuery(id+"F24.imprint","INTERSECT",VERTEX,{"derivedFrom":[makeQuery(id+"F11.boolean.opBoolean","COPY",EDGE,{"derivedFrom":makeQuery(id+"F11.opExtrude","CAP_EDGE",EDGE,{"disambiguationData":[OSD([subQ2])],"isStart":true})}),makeQuery(id+"F11.boolean.opBoolean","SPLIT",EDGE,{"disambiguationData":[TD([makeQuery(id+"F11.opExtrude","SWEPT_FACE",FACE,{"disambiguationData":[OSD([sQuery(id+"F10.wireOp",EDGE,"E43")])]})])],"derivedFrom":makeQuery(id+"F1.opExtrude","CAP_EDGE",EDGE,{"disambiguationData":[OSD([subQ0])],"isStart":false})})]})])]})]});}
            var Q20;
            {var subQ0=sQuery(id+"F8.wireOp",EDGE,"E25");var subQ4=sQuery(id+"F0.wireOp",EDGE,"E0.left");Q20=makeQuery(id+"F13.boolean.opBoolean","INTERSECT",EDGE,{"derivedFrom":[makeQuery(id+"F11.boolean.opBoolean","SPLIT",FACE,{"disambiguationData":[TD([makeQuery(id+"F9.opExtrude","SWEPT_FACE",FACE,{"disambiguationData":[OSD([subQ0])]})])],"derivedFrom":makeQuery(id+"F1.opExtrude","SWEPT_FACE",FACE,{"disambiguationData":[OSD([subQ4])]})}),makeQuery(id+"F13.opExtrude","SWEPT_FACE",FACE,{"disambiguationData":[OSD([sQuery(id+"F12.wireOp",EDGE,"E60.filletArc")])]})]});}
            var Q21;
            {var subQ0=sQuery(id+"F10.wireOp",EDGE,"E43");var subQ1=sQuery(id+"F0.wireOp",EDGE,"E0.left");Q21=makeQuery(id+"F25.boolean.opBoolean","MERGE",EDGE,{"derivedFrom":[makeQuery(id+"F11.boolean.opBoolean","INTERSECT",EDGE,{"derivedFrom":[makeQuery(id+"F1.opExtrude","SWEPT_FACE",FACE,{"disambiguationData":[OSD([subQ1])]}),makeQuery(id+"F11.opExtrude","SWEPT_FACE",FACE,{"disambiguationData":[OSD([subQ0])]})]})],"fromTools":[makeQuery(id+"F25.opExtrude","SWEPT_EDGE",EDGE,{"disambiguationData":[OSD([subQ1,subQ0])]})]});}
            var Q22;
            Q22=makeQuery(id+"F11.boolean.opBoolean","INTERSECT",EDGE,{"derivedFrom":[makeQuery(id+"F1.opExtrude","SWEPT_FACE",FACE,{"disambiguationData":[OSD([sQuery(id+"F0.wireOp",EDGE,"E0.bottom")])]}),makeQuery(id+"F11.opExtrude","SWEPT_FACE",FACE,{"disambiguationData":[OSD([sQuery(id+"F10.wireOp",EDGE,"E43")])]})]});
            var Q23;
            Q23=makeQuery(id+"F7.boolean.opBoolean","COPY",EDGE,{"derivedFrom":makeQuery(id+"F7.opExtrude","CAP_EDGE",EDGE,{"disambiguationData":[OSD([sQuery(id+"F6.wireOp",EDGE,"E16.0")])],"isStart":true})});
            var Q24;
            Q24=makeQuery(id+"F11.boolean.opBoolean","INTERSECT",EDGE,{"derivedFrom":[makeQuery(id+"F1.opExtrude","SWEPT_FACE",FACE,{"disambiguationData":[OSD([sQuery(id+"F0.wireOp",EDGE,"E0.bottom")])]}),makeQuery(id+"F11.opExtrude","SWEPT_FACE",FACE,{"disambiguationData":[OSD([sQuery(id+"F10.wireOp",EDGE,"E44")])]})]});
            var Q25;
            {var subQ0=sQuery(id+"F10.wireOp",EDGE,"E44");var subQ1=sQuery(id+"F0.wireOp",EDGE,"E0.right");Q25=makeQuery(id+"F25.boolean.opBoolean","MERGE",EDGE,{"derivedFrom":[makeQuery(id+"F11.boolean.opBoolean","INTERSECT",EDGE,{"derivedFrom":[makeQuery(id+"F1.opExtrude","SWEPT_FACE",FACE,{"disambiguationData":[OSD([subQ1])]}),makeQuery(id+"F11.opExtrude","SWEPT_FACE",FACE,{"disambiguationData":[OSD([subQ0])]})]})],"fromTools":[makeQuery(id+"F25.opExtrude","SWEPT_EDGE",EDGE,{"disambiguationData":[OSD([subQ1,subQ0])]})]});}
            var Q26;
            Q26=makeQuery(id+"F13.boolean.opBoolean","COPY",EDGE,{"derivedFrom":makeQuery(id+"F13.opExtrude","CAP_EDGE",EDGE,{"disambiguationData":[OSD([sQuery(id+"F12.wireOp",EDGE,"E56.0")])],"isStart":true})});
            var Q27;
            Q27=makeQuery(id+"F13.boolean.opBoolean","COPY",EDGE,{"derivedFrom":makeQuery(id+"F13.opExtrude","CAP_EDGE",EDGE,{"disambiguationData":[OSD([sQuery(id+"F12.wireOp",EDGE,"E52.filletArc")])],"isStart":true})});
            var Q28;
            {var subQ0=sQuery(id+"F0.wireOp",EDGE,"E0.right");var subQ1=makeQuery(id+"F1.opExtrude","SWEPT_FACE",FACE,{"disambiguationData":[OSD([subQ0])]});var subQ2=sQuery(id+"F10.wireOp",EDGE,"E42");var subQ3=makeQuery(id+"F11.opExtrude","SWEPT_FACE",FACE,{"disambiguationData":[OSD([subQ2])]});Q28=makeQuery(id+"F25.boolean.opBoolean","MERGE",EDGE,{"derivedFrom":[makeQuery(id+"F11.boolean.opBoolean","INTERSECT",EDGE,{"disambiguationData":[OD(1.0)],"derivedFrom":[subQ1,subQ3]})],"fromTools":[makeQuery(id+"F25.opExtrude","SWEPT_EDGE",EDGE,{"disambiguationData":[OSD([subQ0,subQ2]),TDD([makeQuery(id+"F24.imprint","INTERSECT",VERTEX,{"derivedFrom":[makeQuery(id+"F11.boolean.opBoolean","COPY",EDGE,{"derivedFrom":makeQuery(id+"F11.opExtrude","CAP_EDGE",EDGE,{"disambiguationData":[OSD([subQ2])],"isStart":true})}),makeQuery(id+"F11.boolean.opBoolean","SPLIT",EDGE,{"disambiguationData":[TD([makeQuery(id+"F11.opExtrude","SWEPT_FACE",FACE,{"disambiguationData":[OSD([sQuery(id+"F10.wireOp",EDGE,"E44")])]})])],"derivedFrom":makeQuery(id+"F1.opExtrude","CAP_EDGE",EDGE,{"disambiguationData":[OSD([subQ0])],"isStart":false})})]})])]})]});}
            var Q29;
            {var subQ0=sQuery(id+"F0.wireOp",EDGE,"E0.right");var subQ1=makeQuery(id+"F1.opExtrude","SWEPT_FACE",FACE,{"disambiguationData":[OSD([subQ0])]});var subQ2=sQuery(id+"F10.wireOp",EDGE,"E42");var subQ3=makeQuery(id+"F11.opExtrude","SWEPT_FACE",FACE,{"disambiguationData":[OSD([subQ2])]});Q29=makeQuery(id+"F25.boolean.opBoolean","MERGE",EDGE,{"derivedFrom":[makeQuery(id+"F11.boolean.opBoolean","INTERSECT",EDGE,{"disambiguationData":[OD(0.0)],"derivedFrom":[subQ1,subQ3]})],"fromTools":[makeQuery(id+"F25.opExtrude","SWEPT_EDGE",EDGE,{"disambiguationData":[OSD([subQ0,subQ2]),TDD([makeQuery(id+"F24.imprint","INTERSECT",VERTEX,{"derivedFrom":[makeQuery(id+"F11.boolean.opBoolean","COPY",EDGE,{"derivedFrom":makeQuery(id+"F11.opExtrude","CAP_EDGE",EDGE,{"disambiguationData":[OSD([subQ2])],"isStart":true})}),makeQuery(id+"F11.boolean.opBoolean","SPLIT",EDGE,{"disambiguationData":[TD([makeQuery(id+"F11.opExtrude","SWEPT_FACE",FACE,{"disambiguationData":[OSD([sQuery(id+"F10.wireOp",EDGE,"E39")])]})])],"derivedFrom":makeQuery(id+"F1.opExtrude","CAP_EDGE",EDGE,{"disambiguationData":[OSD([subQ0])],"isStart":false})})]})])]})]});}
            var Q30;
            Q30=makeQuery(id+"F11.boolean.opBoolean","INTERSECT",EDGE,{"derivedFrom":[makeQuery(id+"F1.opExtrude","SWEPT_FACE",FACE,{"disambiguationData":[OSD([sQuery(id+"F0.wireOp",EDGE,"E0.top")])]}),makeQuery(id+"F11.opExtrude","SWEPT_FACE",FACE,{"disambiguationData":[OSD([sQuery(id+"F10.wireOp",EDGE,"E39")])]})]});
            var Q31;
            {var subQ0=sQuery(id+"F10.wireOp",EDGE,"E39");var subQ1=sQuery(id+"F0.wireOp",EDGE,"E0.right");Q31=makeQuery(id+"F25.boolean.opBoolean","MERGE",EDGE,{"derivedFrom":[makeQuery(id+"F11.boolean.opBoolean","INTERSECT",EDGE,{"derivedFrom":[makeQuery(id+"F1.opExtrude","SWEPT_FACE",FACE,{"disambiguationData":[OSD([subQ1])]}),makeQuery(id+"F11.opExtrude","SWEPT_FACE",FACE,{"disambiguationData":[OSD([subQ0])]})]})],"fromTools":[makeQuery(id+"F25.opExtrude","SWEPT_EDGE",EDGE,{"disambiguationData":[OSD([subQ1,subQ0])]})]});}
            fillet(context, id + "F26", {"entities" : qUnion([Q0, Q1, Q2, Q3, Q4, Q5, Q6, Q7, Q8, Q9, Q10, Q11, Q12, Q13, Q14, Q15, Q16, Q17, Q18, Q19, Q20, Q21, Q22, Q23, Q24, Q25, Q26, Q27, Q28, Q29, Q30, Q31]), "radius" : 1.52 * mm, "tangentPropagation" : true, "allowEdgeOverflow" : false});
        }
        {
            var Q0;
            {var subQ0=sQuery(id+"F0.wireOp",EDGE,"E0.right");var subQ1=makeQuery(id+"F1.opExtrude","SWEPT_FACE",FACE,{"disambiguationData":[OSD([subQ0])]});var subQ2=sQuery(id+"F10.wireOp",EDGE,"E42");var subQ3=makeQuery(id+"F11.opExtrude","SWEPT_FACE",FACE,{"disambiguationData":[OSD([subQ2])]});Q0=makeQuery(id+"F26.opFillet","BLEND_EDGE",EDGE,{"blendedFrom":[makeQuery(id+"F25.boolean.opBoolean","MERGE",EDGE,{"derivedFrom":[makeQuery(id+"F11.boolean.opBoolean","INTERSECT",EDGE,{"disambiguationData":[OD(0.0)],"derivedFrom":[subQ1,subQ3]})],"fromTools":[makeQuery(id+"F25.opExtrude","SWEPT_EDGE",EDGE,{"disambiguationData":[OSD([subQ0,subQ2]),TDD([makeQuery(id+"F24.imprint","INTERSECT",VERTEX,{"derivedFrom":[makeQuery(id+"F11.boolean.opBoolean","COPY",EDGE,{"derivedFrom":makeQuery(id+"F11.opExtrude","CAP_EDGE",EDGE,{"disambiguationData":[OSD([subQ2])],"isStart":true})}),makeQuery(id+"F11.boolean.opBoolean","SPLIT",EDGE,{"disambiguationData":[TD([makeQuery(id+"F11.opExtrude","SWEPT_FACE",FACE,{"disambiguationData":[OSD([sQuery(id+"F10.wireOp",EDGE,"E39")])]})])],"derivedFrom":makeQuery(id+"F1.opExtrude","CAP_EDGE",EDGE,{"disambiguationData":[OSD([subQ0])],"isStart":false})})]})])]})]}),makeQuery(id+"F9.opExtrude","SWEPT_FACE",FACE,{"disambiguationData":[OSD([sQuery(id+"F8.wireOp",EDGE,"E27")])]})],"blendedInto":[makeQuery(id+"F9.opExtrude","SWEPT_FACE",FACE,{"disambiguationData":[OSD([sQuery(id+"F8.wireOp",EDGE,"E27")])]})]});}
            var Q1;
            {var subQ0=sQuery(id+"F0.wireOp",EDGE,"E0.right");var subQ1=makeQuery(id+"F1.opExtrude","SWEPT_FACE",FACE,{"disambiguationData":[OSD([subQ0])]});var subQ2=sQuery(id+"F10.wireOp",EDGE,"E42");var subQ3=makeQuery(id+"F11.opExtrude","SWEPT_FACE",FACE,{"disambiguationData":[OSD([subQ2])]});Q1=makeQuery(id+"F26.opFillet","BLEND_EDGE",EDGE,{"blendedFrom":[makeQuery(id+"F25.boolean.opBoolean","MERGE",EDGE,{"derivedFrom":[makeQuery(id+"F11.boolean.opBoolean","INTERSECT",EDGE,{"disambiguationData":[OD(1.0)],"derivedFrom":[subQ1,subQ3]})],"fromTools":[makeQuery(id+"F25.opExtrude","SWEPT_EDGE",EDGE,{"disambiguationData":[OSD([subQ0,subQ2]),TDD([makeQuery(id+"F24.imprint","INTERSECT",VERTEX,{"derivedFrom":[makeQuery(id+"F11.boolean.opBoolean","COPY",EDGE,{"derivedFrom":makeQuery(id+"F11.opExtrude","CAP_EDGE",EDGE,{"disambiguationData":[OSD([subQ2])],"isStart":true})}),makeQuery(id+"F11.boolean.opBoolean","SPLIT",EDGE,{"disambiguationData":[TD([makeQuery(id+"F11.opExtrude","SWEPT_FACE",FACE,{"disambiguationData":[OSD([sQuery(id+"F10.wireOp",EDGE,"E44")])]})])],"derivedFrom":makeQuery(id+"F1.opExtrude","CAP_EDGE",EDGE,{"disambiguationData":[OSD([subQ0])],"isStart":false})})]})])]})]}),makeQuery(id+"F9.opExtrude","SWEPT_FACE",FACE,{"disambiguationData":[OSD([sQuery(id+"F8.wireOp",EDGE,"E27")])]})],"blendedInto":[makeQuery(id+"F9.opExtrude","SWEPT_FACE",FACE,{"disambiguationData":[OSD([sQuery(id+"F8.wireOp",EDGE,"E27")])]})]});}
            var Q2;
            {var subQ0=sQuery(id+"F10.wireOp",EDGE,"E39");var subQ1=sQuery(id+"F0.wireOp",EDGE,"E0.right");Q2=makeQuery(id+"F26.opFillet","BLEND_EDGE",EDGE,{"blendedFrom":[makeQuery(id+"F25.boolean.opBoolean","MERGE",EDGE,{"derivedFrom":[makeQuery(id+"F11.boolean.opBoolean","INTERSECT",EDGE,{"derivedFrom":[makeQuery(id+"F1.opExtrude","SWEPT_FACE",FACE,{"disambiguationData":[OSD([subQ1])]}),makeQuery(id+"F11.opExtrude","SWEPT_FACE",FACE,{"disambiguationData":[OSD([subQ0])]})]})],"fromTools":[makeQuery(id+"F25.opExtrude","SWEPT_EDGE",EDGE,{"disambiguationData":[OSD([subQ1,subQ0])]})]}),makeQuery(id+"F9.opExtrude","SWEPT_FACE",FACE,{"disambiguationData":[OSD([sQuery(id+"F8.wireOp",EDGE,"E24")])]})],"blendedInto":[makeQuery(id+"F9.opExtrude","SWEPT_FACE",FACE,{"disambiguationData":[OSD([sQuery(id+"F8.wireOp",EDGE,"E24")])]})]});}
            var Q3;
            Q3=makeQuery(id+"F26.opFillet","BLEND_EDGE",EDGE,{"blendedFrom":[makeQuery(id+"F11.boolean.opBoolean","INTERSECT",EDGE,{"derivedFrom":[makeQuery(id+"F1.opExtrude","SWEPT_FACE",FACE,{"disambiguationData":[OSD([sQuery(id+"F0.wireOp",EDGE,"E0.top")])]}),makeQuery(id+"F11.opExtrude","SWEPT_FACE",FACE,{"disambiguationData":[OSD([sQuery(id+"F10.wireOp",EDGE,"E39")])]})]}),makeQuery(id+"F9.opExtrude","SWEPT_FACE",FACE,{"disambiguationData":[OSD([sQuery(id+"F8.wireOp",EDGE,"E24")])]})],"blendedInto":[makeQuery(id+"F9.opExtrude","SWEPT_FACE",FACE,{"disambiguationData":[OSD([sQuery(id+"F8.wireOp",EDGE,"E24")])]})]});
            var Q4;
            Q4=makeQuery(id+"F26.opFillet","BLEND_EDGE",EDGE,{"blendedFrom":[makeQuery(id+"F11.boolean.opBoolean","INTERSECT",EDGE,{"derivedFrom":[makeQuery(id+"F1.opExtrude","SWEPT_FACE",FACE,{"disambiguationData":[OSD([sQuery(id+"F0.wireOp",EDGE,"E0.top")])]}),makeQuery(id+"F11.opExtrude","SWEPT_FACE",FACE,{"disambiguationData":[OSD([sQuery(id+"F10.wireOp",EDGE,"E40")])]})]}),makeQuery(id+"F9.opExtrude","SWEPT_FACE",FACE,{"disambiguationData":[OSD([sQuery(id+"F8.wireOp",EDGE,"E23")])]})],"blendedInto":[makeQuery(id+"F9.opExtrude","SWEPT_FACE",FACE,{"disambiguationData":[OSD([sQuery(id+"F8.wireOp",EDGE,"E23")])]})]});
            var Q5;
            {var subQ0=sQuery(id+"F10.wireOp",EDGE,"E40");var subQ1=sQuery(id+"F0.wireOp",EDGE,"E0.left");Q5=makeQuery(id+"F26.opFillet","BLEND_EDGE",EDGE,{"blendedFrom":[makeQuery(id+"F25.boolean.opBoolean","MERGE",EDGE,{"derivedFrom":[makeQuery(id+"F11.boolean.opBoolean","INTERSECT",EDGE,{"derivedFrom":[makeQuery(id+"F1.opExtrude","SWEPT_FACE",FACE,{"disambiguationData":[OSD([subQ1])]}),makeQuery(id+"F11.opExtrude","SWEPT_FACE",FACE,{"disambiguationData":[OSD([subQ0])]})]})],"fromTools":[makeQuery(id+"F25.opExtrude","SWEPT_EDGE",EDGE,{"disambiguationData":[OSD([subQ1,subQ0])]})]}),makeQuery(id+"F9.opExtrude","SWEPT_FACE",FACE,{"disambiguationData":[OSD([sQuery(id+"F8.wireOp",EDGE,"E23")])]})],"blendedInto":[makeQuery(id+"F9.opExtrude","SWEPT_FACE",FACE,{"disambiguationData":[OSD([sQuery(id+"F8.wireOp",EDGE,"E23")])]})]});}
            var Q6;
            {var subQ0=sQuery(id+"F0.wireOp",EDGE,"E0.left");var subQ1=makeQuery(id+"F1.opExtrude","SWEPT_FACE",FACE,{"disambiguationData":[OSD([subQ0])]});var subQ2=sQuery(id+"F10.wireOp",EDGE,"E41");var subQ3=makeQuery(id+"F11.opExtrude","SWEPT_FACE",FACE,{"disambiguationData":[OSD([subQ2])]});Q6=makeQuery(id+"F26.opFillet","BLEND_EDGE",EDGE,{"blendedFrom":[makeQuery(id+"F25.boolean.opBoolean","MERGE",EDGE,{"derivedFrom":[makeQuery(id+"F11.boolean.opBoolean","INTERSECT",EDGE,{"disambiguationData":[OD(0.0)],"derivedFrom":[subQ1,subQ3]})],"fromTools":[makeQuery(id+"F25.opExtrude","SWEPT_EDGE",EDGE,{"disambiguationData":[OSD([subQ0,subQ2]),TDD([makeQuery(id+"F24.imprint","INTERSECT",VERTEX,{"derivedFrom":[makeQuery(id+"F11.boolean.opBoolean","COPY",EDGE,{"derivedFrom":makeQuery(id+"F11.opExtrude","CAP_EDGE",EDGE,{"disambiguationData":[OSD([subQ2])],"isStart":true})}),makeQuery(id+"F11.boolean.opBoolean","SPLIT",EDGE,{"disambiguationData":[TD([makeQuery(id+"F11.opExtrude","SWEPT_FACE",FACE,{"disambiguationData":[OSD([sQuery(id+"F10.wireOp",EDGE,"E40")])]})])],"derivedFrom":makeQuery(id+"F1.opExtrude","CAP_EDGE",EDGE,{"disambiguationData":[OSD([subQ0])],"isStart":false})})]})])]})]}),makeQuery(id+"F9.opExtrude","SWEPT_FACE",FACE,{"disambiguationData":[OSD([sQuery(id+"F8.wireOp",EDGE,"E28")])]})],"blendedInto":[makeQuery(id+"F9.opExtrude","SWEPT_FACE",FACE,{"disambiguationData":[OSD([sQuery(id+"F8.wireOp",EDGE,"E28")])]})]});}
            var Q7;
            {var subQ0=sQuery(id+"F0.wireOp",EDGE,"E0.left");var subQ1=makeQuery(id+"F1.opExtrude","SWEPT_FACE",FACE,{"disambiguationData":[OSD([subQ0])]});var subQ2=sQuery(id+"F10.wireOp",EDGE,"E41");var subQ3=makeQuery(id+"F11.opExtrude","SWEPT_FACE",FACE,{"disambiguationData":[OSD([subQ2])]});Q7=makeQuery(id+"F26.opFillet","BLEND_EDGE",EDGE,{"blendedFrom":[makeQuery(id+"F25.boolean.opBoolean","MERGE",EDGE,{"derivedFrom":[makeQuery(id+"F11.boolean.opBoolean","INTERSECT",EDGE,{"disambiguationData":[OD(1.0)],"derivedFrom":[subQ1,subQ3]})],"fromTools":[makeQuery(id+"F25.opExtrude","SWEPT_EDGE",EDGE,{"disambiguationData":[OSD([subQ0,subQ2]),TDD([makeQuery(id+"F24.imprint","INTERSECT",VERTEX,{"derivedFrom":[makeQuery(id+"F11.boolean.opBoolean","COPY",EDGE,{"derivedFrom":makeQuery(id+"F11.opExtrude","CAP_EDGE",EDGE,{"disambiguationData":[OSD([subQ2])],"isStart":true})}),makeQuery(id+"F11.boolean.opBoolean","SPLIT",EDGE,{"disambiguationData":[TD([makeQuery(id+"F11.opExtrude","SWEPT_FACE",FACE,{"disambiguationData":[OSD([sQuery(id+"F10.wireOp",EDGE,"E43")])]})])],"derivedFrom":makeQuery(id+"F1.opExtrude","CAP_EDGE",EDGE,{"disambiguationData":[OSD([subQ0])],"isStart":false})})]})])]})]}),makeQuery(id+"F9.opExtrude","SWEPT_FACE",FACE,{"disambiguationData":[OSD([sQuery(id+"F8.wireOp",EDGE,"E28")])]})],"blendedInto":[makeQuery(id+"F9.opExtrude","SWEPT_FACE",FACE,{"disambiguationData":[OSD([sQuery(id+"F8.wireOp",EDGE,"E28")])]})]});}
            var Q8;
            {var subQ0=sQuery(id+"F10.wireOp",EDGE,"E43");var subQ1=sQuery(id+"F0.wireOp",EDGE,"E0.left");Q8=makeQuery(id+"F26.opFillet","BLEND_EDGE",EDGE,{"blendedFrom":[makeQuery(id+"F25.boolean.opBoolean","MERGE",EDGE,{"derivedFrom":[makeQuery(id+"F11.boolean.opBoolean","INTERSECT",EDGE,{"derivedFrom":[makeQuery(id+"F1.opExtrude","SWEPT_FACE",FACE,{"disambiguationData":[OSD([subQ1])]}),makeQuery(id+"F11.opExtrude","SWEPT_FACE",FACE,{"disambiguationData":[OSD([subQ0])]})]})],"fromTools":[makeQuery(id+"F25.opExtrude","SWEPT_EDGE",EDGE,{"disambiguationData":[OSD([subQ1,subQ0])]})]}),makeQuery(id+"F9.opExtrude","SWEPT_FACE",FACE,{"disambiguationData":[OSD([sQuery(id+"F8.wireOp",EDGE,"E25")])]})],"blendedInto":[makeQuery(id+"F9.opExtrude","SWEPT_FACE",FACE,{"disambiguationData":[OSD([sQuery(id+"F8.wireOp",EDGE,"E25")])]})]});}
            var Q9;
            Q9=makeQuery(id+"F26.opFillet","BLEND_EDGE",EDGE,{"blendedFrom":[makeQuery(id+"F11.boolean.opBoolean","INTERSECT",EDGE,{"derivedFrom":[makeQuery(id+"F1.opExtrude","SWEPT_FACE",FACE,{"disambiguationData":[OSD([sQuery(id+"F0.wireOp",EDGE,"E0.bottom")])]}),makeQuery(id+"F11.opExtrude","SWEPT_FACE",FACE,{"disambiguationData":[OSD([sQuery(id+"F10.wireOp",EDGE,"E43")])]})]}),makeQuery(id+"F9.opExtrude","SWEPT_FACE",FACE,{"disambiguationData":[OSD([sQuery(id+"F8.wireOp",EDGE,"E25")])]})],"blendedInto":[makeQuery(id+"F9.opExtrude","SWEPT_FACE",FACE,{"disambiguationData":[OSD([sQuery(id+"F8.wireOp",EDGE,"E25")])]})]});
            var Q10;
            Q10=makeQuery(id+"F26.opFillet","BLEND_EDGE",EDGE,{"blendedFrom":[makeQuery(id+"F11.boolean.opBoolean","INTERSECT",EDGE,{"derivedFrom":[makeQuery(id+"F1.opExtrude","SWEPT_FACE",FACE,{"disambiguationData":[OSD([sQuery(id+"F0.wireOp",EDGE,"E0.bottom")])]}),makeQuery(id+"F11.opExtrude","SWEPT_FACE",FACE,{"disambiguationData":[OSD([sQuery(id+"F10.wireOp",EDGE,"E44")])]})]}),makeQuery(id+"F9.opExtrude","SWEPT_FACE",FACE,{"disambiguationData":[OSD([sQuery(id+"F8.wireOp",EDGE,"E26")])]})],"blendedInto":[makeQuery(id+"F9.opExtrude","SWEPT_FACE",FACE,{"disambiguationData":[OSD([sQuery(id+"F8.wireOp",EDGE,"E26")])]})]});
            var Q11;
            {var subQ0=sQuery(id+"F10.wireOp",EDGE,"E44");var subQ1=sQuery(id+"F0.wireOp",EDGE,"E0.right");Q11=makeQuery(id+"F26.opFillet","BLEND_EDGE",EDGE,{"blendedFrom":[makeQuery(id+"F25.boolean.opBoolean","MERGE",EDGE,{"derivedFrom":[makeQuery(id+"F11.boolean.opBoolean","INTERSECT",EDGE,{"derivedFrom":[makeQuery(id+"F1.opExtrude","SWEPT_FACE",FACE,{"disambiguationData":[OSD([subQ1])]}),makeQuery(id+"F11.opExtrude","SWEPT_FACE",FACE,{"disambiguationData":[OSD([subQ0])]})]})],"fromTools":[makeQuery(id+"F25.opExtrude","SWEPT_EDGE",EDGE,{"disambiguationData":[OSD([subQ1,subQ0])]})]}),makeQuery(id+"F9.opExtrude","SWEPT_FACE",FACE,{"disambiguationData":[OSD([sQuery(id+"F8.wireOp",EDGE,"E26")])]})],"blendedInto":[makeQuery(id+"F9.opExtrude","SWEPT_FACE",FACE,{"disambiguationData":[OSD([sQuery(id+"F8.wireOp",EDGE,"E26")])]})]});}
            fillet(context, id + "F27", {"entities" : qUnion([Q0, Q1, Q2, Q3, Q4, Q5, Q6, Q7, Q8, Q9, Q10, Q11]), "radius" : 3.17 * mm, "tangentPropagation" : true, "allowEdgeOverflow" : false});
        }
        {
            var Q0;
            {var subQ1=sQuery(id+"F0.wireOp",EDGE,"E0.top");var subQ2=sQuery(id+"F10.wireOp",EDGE,"E40");var subQ3=makeQuery(id+"F11.opExtrude","SWEPT_FACE",FACE,{"disambiguationData":[OSD([subQ2])]});var subQ9=sQuery(id+"F24.wireOp",EDGE,"E108.5");var subQ11=sQuery(id+"F8.wireOp",EDGE,"E23");var subQ12=makeQuery(id+"F9.opExtrude","SWEPT_FACE",FACE,{"disambiguationData":[OSD([subQ11])]});var subQ14=makeQuery(id+"F1.opExtrude","SWEPT_FACE",FACE,{"disambiguationData":[OSD([subQ1])]});var subQ18=makeQuery(id+"F11.boolean.opBoolean","MERGE",FACE,{"derivedFrom":[makeQuery(id+"F9.opExtrude","CAP_FACE",FACE,{"disambiguationData":[OSD([subQ11,sQuery(id+"F8.wireOp",EDGE,"E30.trimOffspring"),sQuery(id+"F8.wireOp",EDGE,"E36.0")])],"isStart":false})],"fromTools":[makeQuery(id+"F11.opExtrude","CAP_FACE",FACE,{"disambiguationData":[OSD([subQ2])],"isStart":false})]});Q0=makeQuery(id+"F27.opFillet","TWEAK_EDGE",EDGE,{"derivedFrom":[makeQuery(id+"F26.opFillet","BLEND_VERTEX",VERTEX,{"blendedFrom":[makeQuery(id+"F11.boolean.opBoolean","INTERSECT",EDGE,{"derivedFrom":[subQ14,subQ3]}),subQ12,makeQuery(id+"F25.boolean.opBoolean","SPLIT",FACE,{"disambiguationData":[TD([makeQuery(id+"F25.opExtrude","SWEPT_FACE",FACE,{"disambiguationData":[OSD([subQ9])]})])],"derivedFrom":subQ18}),makeQuery(id+"F25.boolean.opBoolean","SPLIT",FACE,{"disambiguationData":[TD([subQ14])],"derivedFrom":subQ18})],"blendedInto":[subQ12,makeQuery(id+"F25.boolean.opBoolean","SPLIT",FACE,{"disambiguationData":[TD([makeQuery(id+"F25.opExtrude","SWEPT_FACE",FACE,{"disambiguationData":[OSD([subQ9])]})])],"derivedFrom":subQ18}),makeQuery(id+"F25.boolean.opBoolean","SPLIT",FACE,{"disambiguationData":[TD([subQ14])],"derivedFrom":subQ18})]})]});}
            var Q1;
            {var subQ1=sQuery(id+"F10.wireOp",EDGE,"E40");var subQ4=sQuery(id+"F24.wireOp",EDGE,"E108.5");Q1=makeQuery(id+"F25.boolean.opBoolean","SPLIT",EDGE,{"disambiguationData":[TD([makeQuery(id+"F25.opExtrude","SWEPT_FACE",FACE,{"disambiguationData":[OSD([subQ4])]})])],"derivedFrom":makeQuery(id+"F11.boolean.opBoolean","COPY",EDGE,{"derivedFrom":makeQuery(id+"F11.opExtrude","CAP_EDGE",EDGE,{"disambiguationData":[OSD([subQ1])],"isStart":false})})});}
            var Q2;
            {var subQ1=sQuery(id+"F0.wireOp",EDGE,"E0.top");var subQ2=makeQuery(id+"F1.opExtrude","SWEPT_FACE",FACE,{"disambiguationData":[OSD([subQ1])]});var subQ3=sQuery(id+"F8.wireOp",EDGE,"E24");var subQ6=sQuery(id+"F10.wireOp",EDGE,"E39");var subQ7=makeQuery(id+"F11.opExtrude","SWEPT_FACE",FACE,{"disambiguationData":[OSD([subQ6])]});var subQ13=sQuery(id+"F24.wireOp",EDGE,"E107.1");var subQ17=makeQuery(id+"F11.boolean.opBoolean","MERGE",FACE,{"derivedFrom":[makeQuery(id+"F9.opExtrude","CAP_FACE",FACE,{"disambiguationData":[OSD([subQ3,sQuery(id+"F8.wireOp",EDGE,"E33.trimOffspring"),sQuery(id+"F8.wireOp",EDGE,"E35.0")])],"isStart":false})],"fromTools":[makeQuery(id+"F11.opExtrude","CAP_FACE",FACE,{"disambiguationData":[OSD([subQ6])],"isStart":false})]});Q2=makeQuery(id+"F26.opFillet","BLEND_EDGE",EDGE,{"blendedFrom":[makeQuery(id+"F11.boolean.opBoolean","INTERSECT",EDGE,{"derivedFrom":[subQ2,subQ7]}),makeQuery(id+"F25.boolean.opBoolean","SPLIT",FACE,{"disambiguationData":[TD([makeQuery(id+"F25.opExtrude","SWEPT_FACE",FACE,{"disambiguationData":[OSD([subQ13])]})])],"derivedFrom":subQ17}),makeQuery(id+"F25.boolean.opBoolean","SPLIT",FACE,{"disambiguationData":[TD([subQ2])],"derivedFrom":subQ17})],"blendedInto":[makeQuery(id+"F25.boolean.opBoolean","SPLIT",FACE,{"disambiguationData":[TD([makeQuery(id+"F25.opExtrude","SWEPT_FACE",FACE,{"disambiguationData":[OSD([subQ13])]})])],"derivedFrom":subQ17}),makeQuery(id+"F25.boolean.opBoolean","SPLIT",FACE,{"disambiguationData":[TD([subQ2])],"derivedFrom":subQ17})]});}
            var Q3;
            {var subQ0=sQuery(id+"F10.wireOp",EDGE,"E39");var subQ4=sQuery(id+"F24.wireOp",EDGE,"E107.1");Q3=makeQuery(id+"F25.boolean.opBoolean","SPLIT",EDGE,{"disambiguationData":[TD([makeQuery(id+"F25.opExtrude","SWEPT_FACE",FACE,{"disambiguationData":[OSD([subQ4])]})])],"derivedFrom":makeQuery(id+"F11.boolean.opBoolean","COPY",EDGE,{"derivedFrom":makeQuery(id+"F11.opExtrude","CAP_EDGE",EDGE,{"disambiguationData":[OSD([subQ0])],"isStart":false})})});}
            var Q4;
            {var subQ1=sQuery(id+"F8.wireOp",EDGE,"E27");var subQ2=sQuery(id+"F0.wireOp",EDGE,"E0.right");var subQ4=makeQuery(id+"F1.opExtrude","SWEPT_FACE",FACE,{"disambiguationData":[OSD([subQ2])]});var subQ5=sQuery(id+"F10.wireOp",EDGE,"E39");var subQ6=sQuery(id+"F10.wireOp",EDGE,"E42");var subQ7=makeQuery(id+"F11.opExtrude","SWEPT_FACE",FACE,{"disambiguationData":[OSD([subQ6])]});var subQ8=makeQuery(id+"F1.opExtrude","CAP_EDGE",EDGE,{"disambiguationData":[OSD([subQ2])],"isStart":false});var subQ9=makeQuery(id+"F11.boolean.opBoolean","SPLIT",EDGE,{"disambiguationData":[TD([makeQuery(id+"F11.opExtrude","SWEPT_FACE",FACE,{"disambiguationData":[OSD([subQ5])]})])],"derivedFrom":subQ8});var subQ11=makeQuery(id+"F11.boolean.opBoolean","COPY",EDGE,{"derivedFrom":makeQuery(id+"F11.opExtrude","CAP_EDGE",EDGE,{"disambiguationData":[OSD([subQ6])],"isStart":true})});var subQ12=makeQuery(id+"F24.imprint","INTERSECT",VERTEX,{"derivedFrom":[subQ11,subQ9]});var subQ13=sQuery(id+"F24.wireOp",EDGE,"E110.2");var subQ17=sQuery(id+"F24.wireOp",EDGE,"E110.4");var subQ18=makeQuery(id+"F11.boolean.opBoolean","MERGE",FACE,{"derivedFrom":[makeQuery(id+"F9.opExtrude","CAP_FACE",FACE,{"disambiguationData":[OSD([subQ1,sQuery(id+"F8.wireOp",EDGE,"E34.trimOffspring")])],"isStart":false})],"fromTools":[makeQuery(id+"F11.opExtrude","CAP_FACE",FACE,{"disambiguationData":[OSD([subQ6])],"isStart":false})]});Q4=makeQuery(id+"F26.opFillet","BLEND_EDGE",EDGE,{"blendedFrom":[makeQuery(id+"F25.boolean.opBoolean","MERGE",EDGE,{"derivedFrom":[makeQuery(id+"F11.boolean.opBoolean","INTERSECT",EDGE,{"disambiguationData":[OD(0.0)],"derivedFrom":[subQ4,subQ7]})],"fromTools":[makeQuery(id+"F25.opExtrude","SWEPT_EDGE",EDGE,{"disambiguationData":[OSD([subQ2,subQ6]),TDD([subQ12])]})]}),makeQuery(id+"F25.boolean.opBoolean","SPLIT",FACE,{"disambiguationData":[TD([makeQuery(id+"F25.opExtrude","SWEPT_FACE",FACE,{"disambiguationData":[OSD([subQ13])]})])],"derivedFrom":subQ18}),makeQuery(id+"F25.boolean.opBoolean","SPLIT",FACE,{"disambiguationData":[TD([makeQuery(id+"F25.opExtrude","SWEPT_FACE",FACE,{"disambiguationData":[OSD([subQ17])]})])],"derivedFrom":subQ18}),makeQuery(id+"F25.boolean.opBoolean","SPLIT",FACE,{"disambiguationData":[TD([subQ4])],"derivedFrom":subQ18})],"blendedInto":[makeQuery(id+"F25.boolean.opBoolean","SPLIT",FACE,{"disambiguationData":[TD([makeQuery(id+"F25.opExtrude","SWEPT_FACE",FACE,{"disambiguationData":[OSD([subQ13])]})])],"derivedFrom":subQ18}),makeQuery(id+"F25.boolean.opBoolean","SPLIT",FACE,{"disambiguationData":[TD([makeQuery(id+"F25.opExtrude","SWEPT_FACE",FACE,{"disambiguationData":[OSD([subQ17])]})])],"derivedFrom":subQ18}),makeQuery(id+"F25.boolean.opBoolean","SPLIT",FACE,{"disambiguationData":[TD([subQ4])],"derivedFrom":subQ18})]});}
            var Q5;
            {var subQ1=sQuery(id+"F8.wireOp",EDGE,"E27");var subQ2=sQuery(id+"F0.wireOp",EDGE,"E0.right");var subQ4=makeQuery(id+"F1.opExtrude","SWEPT_FACE",FACE,{"disambiguationData":[OSD([subQ2])]});var subQ6=sQuery(id+"F10.wireOp",EDGE,"E42");var subQ7=makeQuery(id+"F11.opExtrude","SWEPT_FACE",FACE,{"disambiguationData":[OSD([subQ6])]});var subQ8=makeQuery(id+"F1.opExtrude","CAP_EDGE",EDGE,{"disambiguationData":[OSD([subQ2])],"isStart":false});var subQ11=makeQuery(id+"F11.boolean.opBoolean","COPY",EDGE,{"derivedFrom":makeQuery(id+"F11.opExtrude","CAP_EDGE",EDGE,{"disambiguationData":[OSD([subQ6])],"isStart":true})});var subQ13=sQuery(id+"F24.wireOp",EDGE,"E110.2");var subQ14=sQuery(id+"F10.wireOp",EDGE,"E44");var subQ15=makeQuery(id+"F11.boolean.opBoolean","SPLIT",EDGE,{"disambiguationData":[TD([makeQuery(id+"F11.opExtrude","SWEPT_FACE",FACE,{"disambiguationData":[OSD([subQ14])]})])],"derivedFrom":subQ8});var subQ16=makeQuery(id+"F24.imprint","INTERSECT",VERTEX,{"derivedFrom":[subQ11,subQ15]});var subQ17=sQuery(id+"F24.wireOp",EDGE,"E110.4");var subQ18=makeQuery(id+"F11.boolean.opBoolean","MERGE",FACE,{"derivedFrom":[makeQuery(id+"F9.opExtrude","CAP_FACE",FACE,{"disambiguationData":[OSD([subQ1,sQuery(id+"F8.wireOp",EDGE,"E34.trimOffspring")])],"isStart":false})],"fromTools":[makeQuery(id+"F11.opExtrude","CAP_FACE",FACE,{"disambiguationData":[OSD([subQ6])],"isStart":false})]});Q5=makeQuery(id+"F26.opFillet","BLEND_EDGE",EDGE,{"blendedFrom":[makeQuery(id+"F25.boolean.opBoolean","MERGE",EDGE,{"derivedFrom":[makeQuery(id+"F11.boolean.opBoolean","INTERSECT",EDGE,{"disambiguationData":[OD(1.0)],"derivedFrom":[subQ4,subQ7]})],"fromTools":[makeQuery(id+"F25.opExtrude","SWEPT_EDGE",EDGE,{"disambiguationData":[OSD([subQ2,subQ6]),TDD([subQ16])]})]}),makeQuery(id+"F25.boolean.opBoolean","SPLIT",FACE,{"disambiguationData":[TD([makeQuery(id+"F25.opExtrude","SWEPT_FACE",FACE,{"disambiguationData":[OSD([subQ13])]})])],"derivedFrom":subQ18}),makeQuery(id+"F25.boolean.opBoolean","SPLIT",FACE,{"disambiguationData":[TD([makeQuery(id+"F25.opExtrude","SWEPT_FACE",FACE,{"disambiguationData":[OSD([subQ17])]})])],"derivedFrom":subQ18}),makeQuery(id+"F25.boolean.opBoolean","SPLIT",FACE,{"disambiguationData":[TD([subQ4])],"derivedFrom":subQ18})],"blendedInto":[makeQuery(id+"F25.boolean.opBoolean","SPLIT",FACE,{"disambiguationData":[TD([makeQuery(id+"F25.opExtrude","SWEPT_FACE",FACE,{"disambiguationData":[OSD([subQ13])]})])],"derivedFrom":subQ18}),makeQuery(id+"F25.boolean.opBoolean","SPLIT",FACE,{"disambiguationData":[TD([makeQuery(id+"F25.opExtrude","SWEPT_FACE",FACE,{"disambiguationData":[OSD([subQ17])]})])],"derivedFrom":subQ18}),makeQuery(id+"F25.boolean.opBoolean","SPLIT",FACE,{"disambiguationData":[TD([subQ4])],"derivedFrom":subQ18})]});}
            var Q6;
            {var subQ0=sQuery(id+"F0.wireOp",EDGE,"E0.right");var subQ1=sQuery(id+"F0.wireOp",EDGE,"E0.bottom");var subQ2=makeQuery(id+"F1.opExtrude","SWEPT_FACE",FACE,{"disambiguationData":[OSD([subQ0])]});var subQ4=sQuery(id+"F10.wireOp",EDGE,"E44");var subQ5=makeQuery(id+"F11.opExtrude","SWEPT_FACE",FACE,{"disambiguationData":[OSD([subQ4])]});var subQ9=sQuery(id+"F24.wireOp",EDGE,"E112.2");var subQ13=sQuery(id+"F8.wireOp",EDGE,"E26");var subQ16=makeQuery(id+"F11.boolean.opBoolean","MERGE",FACE,{"derivedFrom":[makeQuery(id+"F9.opExtrude","CAP_FACE",FACE,{"disambiguationData":[OSD([subQ13,sQuery(id+"F8.wireOp",EDGE,"E32.0"),sQuery(id+"F8.wireOp",EDGE,"E38.trimOffspring")])],"isStart":false})],"fromTools":[makeQuery(id+"F11.opExtrude","CAP_FACE",FACE,{"disambiguationData":[OSD([subQ4])],"isStart":false})]});Q6=makeQuery(id+"F26.opFillet","BLEND_EDGE",EDGE,{"blendedFrom":[makeQuery(id+"F25.boolean.opBoolean","MERGE",EDGE,{"derivedFrom":[makeQuery(id+"F11.boolean.opBoolean","INTERSECT",EDGE,{"derivedFrom":[subQ2,subQ5]})],"fromTools":[makeQuery(id+"F25.opExtrude","SWEPT_EDGE",EDGE,{"disambiguationData":[OSD([subQ0,subQ4])]})]}),makeQuery(id+"F25.boolean.opBoolean","SPLIT",FACE,{"disambiguationData":[TD([makeQuery(id+"F25.opExtrude","SWEPT_FACE",FACE,{"disambiguationData":[OSD([subQ9])]})])],"derivedFrom":subQ16}),makeQuery(id+"F25.boolean.opBoolean","SPLIT",FACE,{"disambiguationData":[TD([makeQuery(id+"F1.opExtrude","SWEPT_FACE",FACE,{"disambiguationData":[OSD([subQ1])]})])],"derivedFrom":subQ16})],"blendedInto":[makeQuery(id+"F25.boolean.opBoolean","SPLIT",FACE,{"disambiguationData":[TD([makeQuery(id+"F25.opExtrude","SWEPT_FACE",FACE,{"disambiguationData":[OSD([subQ9])]})])],"derivedFrom":subQ16}),makeQuery(id+"F25.boolean.opBoolean","SPLIT",FACE,{"disambiguationData":[TD([makeQuery(id+"F1.opExtrude","SWEPT_FACE",FACE,{"disambiguationData":[OSD([subQ1])]})])],"derivedFrom":subQ16})]});}
            var Q7;
            {var subQ1=sQuery(id+"F0.wireOp",EDGE,"E0.bottom");var subQ4=sQuery(id+"F10.wireOp",EDGE,"E44");var subQ5=makeQuery(id+"F11.opExtrude","SWEPT_FACE",FACE,{"disambiguationData":[OSD([subQ4])]});var subQ9=sQuery(id+"F24.wireOp",EDGE,"E112.2");var subQ13=sQuery(id+"F8.wireOp",EDGE,"E26");var subQ14=makeQuery(id+"F1.opExtrude","SWEPT_FACE",FACE,{"disambiguationData":[OSD([subQ1])]});var subQ17=makeQuery(id+"F11.boolean.opBoolean","MERGE",FACE,{"derivedFrom":[makeQuery(id+"F9.opExtrude","CAP_FACE",FACE,{"disambiguationData":[OSD([subQ13,sQuery(id+"F8.wireOp",EDGE,"E32.0"),sQuery(id+"F8.wireOp",EDGE,"E38.trimOffspring")])],"isStart":false})],"fromTools":[makeQuery(id+"F11.opExtrude","CAP_FACE",FACE,{"disambiguationData":[OSD([subQ4])],"isStart":false})]});Q7=makeQuery(id+"F26.opFillet","BLEND_EDGE",EDGE,{"blendedFrom":[makeQuery(id+"F11.boolean.opBoolean","INTERSECT",EDGE,{"derivedFrom":[subQ14,subQ5]}),makeQuery(id+"F25.boolean.opBoolean","SPLIT",FACE,{"disambiguationData":[TD([makeQuery(id+"F25.opExtrude","SWEPT_FACE",FACE,{"disambiguationData":[OSD([subQ9])]})])],"derivedFrom":subQ17}),makeQuery(id+"F25.boolean.opBoolean","SPLIT",FACE,{"disambiguationData":[TD([subQ14])],"derivedFrom":subQ17})],"blendedInto":[makeQuery(id+"F25.boolean.opBoolean","SPLIT",FACE,{"disambiguationData":[TD([makeQuery(id+"F25.opExtrude","SWEPT_FACE",FACE,{"disambiguationData":[OSD([subQ9])]})])],"derivedFrom":subQ17}),makeQuery(id+"F25.boolean.opBoolean","SPLIT",FACE,{"disambiguationData":[TD([subQ14])],"derivedFrom":subQ17})]});}
            var Q8;
            {var subQ2=sQuery(id+"F0.wireOp",EDGE,"E0.bottom");var subQ3=makeQuery(id+"F1.opExtrude","SWEPT_FACE",FACE,{"disambiguationData":[OSD([subQ2])]});var subQ7=sQuery(id+"F10.wireOp",EDGE,"E43");var subQ8=makeQuery(id+"F11.opExtrude","SWEPT_FACE",FACE,{"disambiguationData":[OSD([subQ7])]});var subQ12=sQuery(id+"F24.wireOp",EDGE,"E111.4");var subQ15=sQuery(id+"F8.wireOp",EDGE,"E25");var subQ17=makeQuery(id+"F11.boolean.opBoolean","MERGE",FACE,{"derivedFrom":[makeQuery(id+"F9.opExtrude","CAP_FACE",FACE,{"disambiguationData":[OSD([subQ15,sQuery(id+"F8.wireOp",EDGE,"E29.0"),sQuery(id+"F8.wireOp",EDGE,"E37.0")])],"isStart":false})],"fromTools":[makeQuery(id+"F11.opExtrude","CAP_FACE",FACE,{"disambiguationData":[OSD([subQ7])],"isStart":false})]});Q8=makeQuery(id+"F26.opFillet","BLEND_EDGE",EDGE,{"blendedFrom":[makeQuery(id+"F11.boolean.opBoolean","INTERSECT",EDGE,{"derivedFrom":[subQ3,subQ8]}),makeQuery(id+"F25.boolean.opBoolean","SPLIT",FACE,{"disambiguationData":[TD([makeQuery(id+"F25.opExtrude","SWEPT_FACE",FACE,{"disambiguationData":[OSD([subQ12])]})])],"derivedFrom":subQ17}),makeQuery(id+"F25.boolean.opBoolean","SPLIT",FACE,{"disambiguationData":[TD([subQ3])],"derivedFrom":subQ17})],"blendedInto":[makeQuery(id+"F25.boolean.opBoolean","SPLIT",FACE,{"disambiguationData":[TD([makeQuery(id+"F25.opExtrude","SWEPT_FACE",FACE,{"disambiguationData":[OSD([subQ12])]})])],"derivedFrom":subQ17}),makeQuery(id+"F25.boolean.opBoolean","SPLIT",FACE,{"disambiguationData":[TD([subQ3])],"derivedFrom":subQ17})]});}
            var Q9;
            {var subQ2=sQuery(id+"F0.wireOp",EDGE,"E0.bottom");var subQ3=sQuery(id+"F0.wireOp",EDGE,"E0.left");var subQ4=makeQuery(id+"F1.opExtrude","SWEPT_FACE",FACE,{"disambiguationData":[OSD([subQ3])]});var subQ6=sQuery(id+"F10.wireOp",EDGE,"E43");var subQ7=makeQuery(id+"F11.opExtrude","SWEPT_FACE",FACE,{"disambiguationData":[OSD([subQ6])]});var subQ11=sQuery(id+"F24.wireOp",EDGE,"E111.4");var subQ14=sQuery(id+"F8.wireOp",EDGE,"E25");var subQ16=makeQuery(id+"F11.boolean.opBoolean","MERGE",FACE,{"derivedFrom":[makeQuery(id+"F9.opExtrude","CAP_FACE",FACE,{"disambiguationData":[OSD([subQ14,sQuery(id+"F8.wireOp",EDGE,"E29.0"),sQuery(id+"F8.wireOp",EDGE,"E37.0")])],"isStart":false})],"fromTools":[makeQuery(id+"F11.opExtrude","CAP_FACE",FACE,{"disambiguationData":[OSD([subQ6])],"isStart":false})]});Q9=makeQuery(id+"F26.opFillet","BLEND_EDGE",EDGE,{"blendedFrom":[makeQuery(id+"F25.boolean.opBoolean","MERGE",EDGE,{"derivedFrom":[makeQuery(id+"F11.boolean.opBoolean","INTERSECT",EDGE,{"derivedFrom":[subQ4,subQ7]})],"fromTools":[makeQuery(id+"F25.opExtrude","SWEPT_EDGE",EDGE,{"disambiguationData":[OSD([subQ3,subQ6])]})]}),makeQuery(id+"F25.boolean.opBoolean","SPLIT",FACE,{"disambiguationData":[TD([makeQuery(id+"F25.opExtrude","SWEPT_FACE",FACE,{"disambiguationData":[OSD([subQ11])]})])],"derivedFrom":subQ16}),makeQuery(id+"F25.boolean.opBoolean","SPLIT",FACE,{"disambiguationData":[TD([makeQuery(id+"F1.opExtrude","SWEPT_FACE",FACE,{"disambiguationData":[OSD([subQ2])]})])],"derivedFrom":subQ16})],"blendedInto":[makeQuery(id+"F25.boolean.opBoolean","SPLIT",FACE,{"disambiguationData":[TD([makeQuery(id+"F25.opExtrude","SWEPT_FACE",FACE,{"disambiguationData":[OSD([subQ11])]})])],"derivedFrom":subQ16}),makeQuery(id+"F25.boolean.opBoolean","SPLIT",FACE,{"disambiguationData":[TD([makeQuery(id+"F1.opExtrude","SWEPT_FACE",FACE,{"disambiguationData":[OSD([subQ2])]})])],"derivedFrom":subQ16})]});}
            var Q10;
            {var subQ1=sQuery(id+"F8.wireOp",EDGE,"E28");var subQ2=sQuery(id+"F0.wireOp",EDGE,"E0.left");var subQ3=makeQuery(id+"F1.opExtrude","SWEPT_FACE",FACE,{"disambiguationData":[OSD([subQ2])]});var subQ5=sQuery(id+"F10.wireOp",EDGE,"E41");var subQ6=makeQuery(id+"F11.opExtrude","SWEPT_FACE",FACE,{"disambiguationData":[OSD([subQ5])]});var subQ8=makeQuery(id+"F1.opExtrude","CAP_EDGE",EDGE,{"disambiguationData":[OSD([subQ2])],"isStart":false});var subQ11=sQuery(id+"F10.wireOp",EDGE,"E40");var subQ12=makeQuery(id+"F11.boolean.opBoolean","SPLIT",EDGE,{"disambiguationData":[TD([makeQuery(id+"F11.opExtrude","SWEPT_FACE",FACE,{"disambiguationData":[OSD([subQ11])]})])],"derivedFrom":subQ8});var subQ13=makeQuery(id+"F11.boolean.opBoolean","COPY",EDGE,{"derivedFrom":makeQuery(id+"F11.opExtrude","CAP_EDGE",EDGE,{"disambiguationData":[OSD([subQ5])],"isStart":true})});var subQ14=makeQuery(id+"F24.imprint","INTERSECT",VERTEX,{"derivedFrom":[subQ13,subQ12]});var subQ15=sQuery(id+"F24.wireOp",EDGE,"E109.4");var subQ17=sQuery(id+"F24.wireOp",EDGE,"E109.2");var subQ18=makeQuery(id+"F11.boolean.opBoolean","MERGE",FACE,{"derivedFrom":[makeQuery(id+"F9.opExtrude","CAP_FACE",FACE,{"disambiguationData":[OSD([subQ1,sQuery(id+"F8.wireOp",EDGE,"E31.trimOffspring")])],"isStart":false})],"fromTools":[makeQuery(id+"F11.opExtrude","CAP_FACE",FACE,{"disambiguationData":[OSD([subQ5])],"isStart":false})]});Q10=makeQuery(id+"F26.opFillet","BLEND_EDGE",EDGE,{"blendedFrom":[makeQuery(id+"F25.boolean.opBoolean","MERGE",EDGE,{"derivedFrom":[makeQuery(id+"F11.boolean.opBoolean","INTERSECT",EDGE,{"disambiguationData":[OD(0.0)],"derivedFrom":[subQ3,subQ6]})],"fromTools":[makeQuery(id+"F25.opExtrude","SWEPT_EDGE",EDGE,{"disambiguationData":[OSD([subQ2,subQ5]),TDD([subQ14])]})]}),makeQuery(id+"F25.boolean.opBoolean","SPLIT",FACE,{"disambiguationData":[TD([makeQuery(id+"F25.opExtrude","SWEPT_FACE",FACE,{"disambiguationData":[OSD([subQ15])]})])],"derivedFrom":subQ18}),makeQuery(id+"F25.boolean.opBoolean","SPLIT",FACE,{"disambiguationData":[TD([makeQuery(id+"F25.opExtrude","SWEPT_FACE",FACE,{"disambiguationData":[OSD([subQ17])]})])],"derivedFrom":subQ18}),makeQuery(id+"F25.boolean.opBoolean","SPLIT",FACE,{"disambiguationData":[TD([subQ3])],"derivedFrom":subQ18})],"blendedInto":[makeQuery(id+"F25.boolean.opBoolean","SPLIT",FACE,{"disambiguationData":[TD([makeQuery(id+"F25.opExtrude","SWEPT_FACE",FACE,{"disambiguationData":[OSD([subQ15])]})])],"derivedFrom":subQ18}),makeQuery(id+"F25.boolean.opBoolean","SPLIT",FACE,{"disambiguationData":[TD([makeQuery(id+"F25.opExtrude","SWEPT_FACE",FACE,{"disambiguationData":[OSD([subQ17])]})])],"derivedFrom":subQ18}),makeQuery(id+"F25.boolean.opBoolean","SPLIT",FACE,{"disambiguationData":[TD([subQ3])],"derivedFrom":subQ18})]});}
            var Q11;
            {var subQ1=sQuery(id+"F8.wireOp",EDGE,"E28");var subQ2=sQuery(id+"F0.wireOp",EDGE,"E0.left");var subQ3=makeQuery(id+"F1.opExtrude","SWEPT_FACE",FACE,{"disambiguationData":[OSD([subQ2])]});var subQ5=sQuery(id+"F10.wireOp",EDGE,"E41");var subQ6=makeQuery(id+"F11.opExtrude","SWEPT_FACE",FACE,{"disambiguationData":[OSD([subQ5])]});var subQ7=sQuery(id+"F10.wireOp",EDGE,"E43");var subQ8=makeQuery(id+"F1.opExtrude","CAP_EDGE",EDGE,{"disambiguationData":[OSD([subQ2])],"isStart":false});var subQ9=makeQuery(id+"F11.boolean.opBoolean","SPLIT",EDGE,{"disambiguationData":[TD([makeQuery(id+"F11.opExtrude","SWEPT_FACE",FACE,{"disambiguationData":[OSD([subQ7])]})])],"derivedFrom":subQ8});var subQ13=makeQuery(id+"F11.boolean.opBoolean","COPY",EDGE,{"derivedFrom":makeQuery(id+"F11.opExtrude","CAP_EDGE",EDGE,{"disambiguationData":[OSD([subQ5])],"isStart":true})});var subQ15=sQuery(id+"F24.wireOp",EDGE,"E109.4");var subQ16=makeQuery(id+"F24.imprint","INTERSECT",VERTEX,{"derivedFrom":[subQ13,subQ9]});var subQ17=sQuery(id+"F24.wireOp",EDGE,"E109.2");var subQ18=makeQuery(id+"F11.boolean.opBoolean","MERGE",FACE,{"derivedFrom":[makeQuery(id+"F9.opExtrude","CAP_FACE",FACE,{"disambiguationData":[OSD([subQ1,sQuery(id+"F8.wireOp",EDGE,"E31.trimOffspring")])],"isStart":false})],"fromTools":[makeQuery(id+"F11.opExtrude","CAP_FACE",FACE,{"disambiguationData":[OSD([subQ5])],"isStart":false})]});Q11=makeQuery(id+"F26.opFillet","BLEND_EDGE",EDGE,{"blendedFrom":[makeQuery(id+"F25.boolean.opBoolean","MERGE",EDGE,{"derivedFrom":[makeQuery(id+"F11.boolean.opBoolean","INTERSECT",EDGE,{"disambiguationData":[OD(1.0)],"derivedFrom":[subQ3,subQ6]})],"fromTools":[makeQuery(id+"F25.opExtrude","SWEPT_EDGE",EDGE,{"disambiguationData":[OSD([subQ2,subQ5]),TDD([subQ16])]})]}),makeQuery(id+"F25.boolean.opBoolean","SPLIT",FACE,{"disambiguationData":[TD([makeQuery(id+"F25.opExtrude","SWEPT_FACE",FACE,{"disambiguationData":[OSD([subQ15])]})])],"derivedFrom":subQ18}),makeQuery(id+"F25.boolean.opBoolean","SPLIT",FACE,{"disambiguationData":[TD([makeQuery(id+"F25.opExtrude","SWEPT_FACE",FACE,{"disambiguationData":[OSD([subQ17])]})])],"derivedFrom":subQ18}),makeQuery(id+"F25.boolean.opBoolean","SPLIT",FACE,{"disambiguationData":[TD([subQ3])],"derivedFrom":subQ18})],"blendedInto":[makeQuery(id+"F25.boolean.opBoolean","SPLIT",FACE,{"disambiguationData":[TD([makeQuery(id+"F25.opExtrude","SWEPT_FACE",FACE,{"disambiguationData":[OSD([subQ15])]})])],"derivedFrom":subQ18}),makeQuery(id+"F25.boolean.opBoolean","SPLIT",FACE,{"disambiguationData":[TD([makeQuery(id+"F25.opExtrude","SWEPT_FACE",FACE,{"disambiguationData":[OSD([subQ17])]})])],"derivedFrom":subQ18}),makeQuery(id+"F25.boolean.opBoolean","SPLIT",FACE,{"disambiguationData":[TD([subQ3])],"derivedFrom":subQ18})]});}
            fillet(context, id + "F28", {"entities" : qUnion([Q0, Q1, Q2, Q3, Q4, Q5, Q6, Q7, Q8, Q9, Q10, Q11]), "radius" : 0.38 * mm, "tangentPropagation" : true, "allowEdgeOverflow" : false});
        }
        {
            var Q0;
            Q0=makeQuery(id+"F9.opExtrude","CAP_EDGE",EDGE,{"disambiguationData":[OSD([sQuery(id+"F8.wireOp",EDGE,"E23")])],"isStart":false});
            var Q1;
            Q1=makeQuery(id+"F9.opExtrude","CAP_EDGE",EDGE,{"disambiguationData":[OSD([sQuery(id+"F8.wireOp",EDGE,"E24")])],"isStart":false});
            var Q2;
            Q2=makeQuery(id+"F9.opExtrude","CAP_EDGE",EDGE,{"disambiguationData":[OSD([sQuery(id+"F8.wireOp",EDGE,"E28")])],"isStart":false});
            var Q3;
            Q3=makeQuery(id+"F9.opExtrude","CAP_EDGE",EDGE,{"disambiguationData":[OSD([sQuery(id+"F8.wireOp",EDGE,"E25")])],"isStart":false});
            var Q4;
            Q4=makeQuery(id+"F9.opExtrude","CAP_EDGE",EDGE,{"disambiguationData":[OSD([sQuery(id+"F8.wireOp",EDGE,"E26")])],"isStart":false});
            var Q5;
            Q5=makeQuery(id+"F9.opExtrude","CAP_EDGE",EDGE,{"disambiguationData":[OSD([sQuery(id+"F8.wireOp",EDGE,"E27")])],"isStart":false});
            fillet(context, id + "F29", {"entities" : qUnion([Q0, Q1, Q2, Q3, Q4, Q5]), "radius" : 0.38 * mm, "tangentPropagation" : true, "allowEdgeOverflow" : false});
        }
        {
            var Q0;
            Q0=makeQuery(id+"F13.boolean.opBoolean","INTERSECT",EDGE,{"derivedFrom":[makeQuery(id+"F3.boolean.opBoolean","COPY",FACE,{"derivedFrom":makeQuery(id+"F3.opExtrude","SWEPT_FACE",FACE,{"disambiguationData":[OSD([sQuery(id+"F2.wireOp",EDGE,"E1.0")])]})}),makeQuery(id+"F13.opExtrude","SWEPT_FACE",FACE,{"disambiguationData":[OSD([sQuery(id+"F12.wireOp",EDGE,"E47.0")])]})]});
            var Q1;
            Q1=makeQuery(id+"F15.boolean.opBoolean","INTERSECT",EDGE,{"derivedFrom":[makeQuery(id+"F3.boolean.opBoolean","COPY",FACE,{"derivedFrom":makeQuery(id+"F3.opExtrude","SWEPT_FACE",FACE,{"disambiguationData":[OSD([sQuery(id+"F2.wireOp",EDGE,"E4.0")])]})}),makeQuery(id+"F15.opExtrude","SWEPT_FACE",FACE,{"disambiguationData":[OSD([sQuery(id+"F14.wireOp",EDGE,"E66.0")])]})]});
            var Q2;
            Q2=makeQuery(id+"F15.boolean.opBoolean","INTERSECT",EDGE,{"derivedFrom":[makeQuery(id+"F3.boolean.opBoolean","COPY",FACE,{"derivedFrom":makeQuery(id+"F3.opExtrude","SWEPT_FACE",FACE,{"disambiguationData":[OSD([sQuery(id+"F2.wireOp",EDGE,"E4.0")])]})}),makeQuery(id+"F15.opExtrude","SWEPT_FACE",FACE,{"disambiguationData":[OSD([sQuery(id+"F14.wireOp",EDGE,"E63.0")])]})]});
            var Q3;
            Q3=makeQuery(id+"F5.boolean.opBoolean","INTERSECT",EDGE,{"derivedFrom":[makeQuery(id+"F3.boolean.opBoolean","COPY",FACE,{"derivedFrom":makeQuery(id+"F3.opExtrude","SWEPT_FACE",FACE,{"disambiguationData":[OSD([sQuery(id+"F2.wireOp",EDGE,"E4.0")])]})}),makeQuery(id+"F5.opExtrude","SWEPT_FACE",FACE,{"disambiguationData":[OSD([sQuery(id+"F4.wireOp",EDGE,"E11.filletArc")])]})]});
            var Q4;
            Q4=makeQuery(id+"F13.boolean.opBoolean","INTERSECT",EDGE,{"derivedFrom":[makeQuery(id+"F3.boolean.opBoolean","COPY",FACE,{"derivedFrom":makeQuery(id+"F3.opExtrude","SWEPT_FACE",FACE,{"disambiguationData":[OSD([sQuery(id+"F2.wireOp",EDGE,"E2.0")])]})}),makeQuery(id+"F13.opExtrude","SWEPT_FACE",FACE,{"disambiguationData":[OSD([sQuery(id+"F12.wireOp",EDGE,"E49.filletArc")])]})]});
            var Q5;
            Q5=makeQuery(id+"F13.boolean.opBoolean","INTERSECT",EDGE,{"derivedFrom":[makeQuery(id+"F3.boolean.opBoolean","COPY",FACE,{"derivedFrom":makeQuery(id+"F3.opExtrude","SWEPT_FACE",FACE,{"disambiguationData":[OSD([sQuery(id+"F2.wireOp",EDGE,"E2.0")])]})}),makeQuery(id+"F13.opExtrude","SWEPT_FACE",FACE,{"disambiguationData":[OSD([sQuery(id+"F12.wireOp",EDGE,"E57.filletArc")])]})]});
            fillet(context, id + "F30", {"entities" : qUnion([Q0, Q1, Q2, Q3, Q4, Q5]), "radius" : 0.38 * mm, "tangentPropagation" : true, "allowEdgeOverflow" : false});
        }
        {
            var Q0;
            Q0=makeQuery(id+"F3.boolean.opBoolean","COPY",EDGE,{"derivedFrom":makeQuery(id+"F3.opExtrude","SWEPT_EDGE",EDGE,{"disambiguationData":[OSD([sQuery(id+"F2.wireOp",EDGE,"E1.0"),sQuery(id+"F2.wireOp",EDGE,"E3.0")])]})});
            var Q1;
            Q1=makeQuery(id+"F3.boolean.opBoolean","COPY",EDGE,{"derivedFrom":makeQuery(id+"F3.opExtrude","SWEPT_EDGE",EDGE,{"disambiguationData":[OSD([sQuery(id+"F2.wireOp",EDGE,"E2.0"),sQuery(id+"F2.wireOp",EDGE,"E3.0")])]})});
            var Q2;
            {var subQ0=sQuery(id+"F2.wireOp",EDGE,"E3.0");var subQ1=makeQuery(id+"F3.boolean.opBoolean","COPY",FACE,{"derivedFrom":makeQuery(id+"F3.opExtrude","SWEPT_FACE",FACE,{"disambiguationData":[OSD([subQ0])]})});var subQ2=sQuery(id+"F2.wireOp",EDGE,"E2.0");Q2=makeQuery(id+"F13.boolean.opBoolean","SPLIT",EDGE,{"disambiguationData":[TD([subQ1])],"derivedFrom":makeQuery(id+"F11.boolean.opBoolean","SPLIT",EDGE,{"disambiguationData":[TD([subQ1])],"derivedFrom":makeQuery(id+"F3.boolean.opBoolean","COPY",EDGE,{"derivedFrom":makeQuery(id+"F3.opExtrude","CAP_EDGE",EDGE,{"disambiguationData":[OSD([subQ2])],"isStart":false})})})});}
            var Q3;
            Q3=makeQuery(id+"F3.boolean.opBoolean","COPY",EDGE,{"derivedFrom":makeQuery(id+"F3.opExtrude","CAP_EDGE",EDGE,{"disambiguationData":[OSD([sQuery(id+"F2.wireOp",EDGE,"E3.0")])],"isStart":false})});
            var Q4;
            {var subQ0=sQuery(id+"F2.wireOp",EDGE,"E3.0");var subQ1=makeQuery(id+"F3.boolean.opBoolean","COPY",FACE,{"derivedFrom":makeQuery(id+"F3.opExtrude","SWEPT_FACE",FACE,{"disambiguationData":[OSD([subQ0])]})});var subQ2=sQuery(id+"F2.wireOp",EDGE,"E1.0");Q4=makeQuery(id+"F13.boolean.opBoolean","SPLIT",EDGE,{"disambiguationData":[TD([subQ1])],"derivedFrom":makeQuery(id+"F11.boolean.opBoolean","SPLIT",EDGE,{"disambiguationData":[TD([subQ1])],"derivedFrom":makeQuery(id+"F3.boolean.opBoolean","COPY",EDGE,{"derivedFrom":makeQuery(id+"F3.opExtrude","CAP_EDGE",EDGE,{"disambiguationData":[OSD([subQ2])],"isStart":false})})})});}
            var Q5;
            {var subQ0=makeQuery(id+"F11.opExtrude","SWEPT_FACE",FACE,{"disambiguationData":[OSD([sQuery(id+"F10.wireOp",EDGE,"E41")])]});var subQ1=sQuery(id+"F2.wireOp",EDGE,"E2.0");var subQ3=sQuery(id+"F2.wireOp",EDGE,"E4.0");Q5=makeQuery(id+"F13.boolean.opBoolean","SPLIT",EDGE,{"disambiguationData":[TD([makeQuery(id+"F11.boolean.opBoolean","COPY",FACE,{"derivedFrom":subQ0})])],"derivedFrom":makeQuery(id+"F11.boolean.opBoolean","SPLIT",EDGE,{"disambiguationData":[TD([makeQuery(id+"F3.boolean.opBoolean","COPY",FACE,{"derivedFrom":makeQuery(id+"F3.opExtrude","SWEPT_FACE",FACE,{"disambiguationData":[OSD([subQ3])]})})])],"derivedFrom":makeQuery(id+"F3.boolean.opBoolean","COPY",EDGE,{"derivedFrom":makeQuery(id+"F3.opExtrude","CAP_EDGE",EDGE,{"disambiguationData":[OSD([subQ1])],"isStart":false})})})});}
            var Q6;
            {var subQ0=makeQuery(id+"F11.opExtrude","SWEPT_FACE",FACE,{"disambiguationData":[OSD([sQuery(id+"F10.wireOp",EDGE,"E41")])]});var subQ1=sQuery(id+"F2.wireOp",EDGE,"E2.0");var subQ3=sQuery(id+"F2.wireOp",EDGE,"E3.0");Q6=makeQuery(id+"F13.boolean.opBoolean","SPLIT",EDGE,{"disambiguationData":[TD([makeQuery(id+"F11.boolean.opBoolean","COPY",FACE,{"derivedFrom":subQ0})])],"derivedFrom":makeQuery(id+"F11.boolean.opBoolean","SPLIT",EDGE,{"disambiguationData":[TD([makeQuery(id+"F3.boolean.opBoolean","COPY",FACE,{"derivedFrom":makeQuery(id+"F3.opExtrude","SWEPT_FACE",FACE,{"disambiguationData":[OSD([subQ3])]})})])],"derivedFrom":makeQuery(id+"F3.boolean.opBoolean","COPY",EDGE,{"derivedFrom":makeQuery(id+"F3.opExtrude","CAP_EDGE",EDGE,{"disambiguationData":[OSD([subQ1])],"isStart":false})})})});}
            var Q7;
            {var subQ0=sQuery(id+"F2.wireOp",EDGE,"E4.0");var subQ1=sQuery(id+"F2.wireOp",EDGE,"E2.0");Q7=makeQuery(id+"F15.boolean.opBoolean","SPLIT",EDGE,{"disambiguationData":[TD([makeQuery(id+"F3.boolean.opBoolean","COPY",FACE,{"derivedFrom":makeQuery(id+"F3.opExtrude","SWEPT_FACE",FACE,{"disambiguationData":[OSD([subQ1])]})})])],"derivedFrom":makeQuery(id+"F3.boolean.opBoolean","COPY",EDGE,{"derivedFrom":makeQuery(id+"F3.opExtrude","CAP_EDGE",EDGE,{"disambiguationData":[OSD([subQ0])],"isStart":false})})});}
            var Q8;
            {var subQ0=sQuery(id+"F2.wireOp",EDGE,"E4.0");var subQ1=makeQuery(id+"F3.boolean.opBoolean","COPY",FACE,{"derivedFrom":makeQuery(id+"F3.opExtrude","SWEPT_FACE",FACE,{"disambiguationData":[OSD([subQ0])]})});var subQ2=sQuery(id+"F2.wireOp",EDGE,"E2.0");Q8=makeQuery(id+"F13.boolean.opBoolean","SPLIT",EDGE,{"disambiguationData":[TD([subQ1])],"derivedFrom":makeQuery(id+"F11.boolean.opBoolean","SPLIT",EDGE,{"disambiguationData":[TD([subQ1])],"derivedFrom":makeQuery(id+"F3.boolean.opBoolean","COPY",EDGE,{"derivedFrom":makeQuery(id+"F3.opExtrude","CAP_EDGE",EDGE,{"disambiguationData":[OSD([subQ2])],"isStart":false})})})});}
            var Q9;
            Q9=makeQuery(id+"F3.boolean.opBoolean","COPY",EDGE,{"derivedFrom":makeQuery(id+"F3.opExtrude","SWEPT_EDGE",EDGE,{"disambiguationData":[OSD([sQuery(id+"F2.wireOp",EDGE,"E2.0"),sQuery(id+"F2.wireOp",EDGE,"E4.0")])]})});
            var Q10;
            Q10=makeQuery(id+"F3.boolean.opBoolean","COPY",EDGE,{"derivedFrom":makeQuery(id+"F3.opExtrude","SWEPT_EDGE",EDGE,{"disambiguationData":[OSD([sQuery(id+"F2.wireOp",EDGE,"E1.0"),sQuery(id+"F2.wireOp",EDGE,"E4.0")])]})});
            var Q11;
            {var subQ0=sQuery(id+"F2.wireOp",EDGE,"E4.0");var subQ1=sQuery(id+"F2.wireOp",EDGE,"E1.0");Q11=makeQuery(id+"F15.boolean.opBoolean","SPLIT",EDGE,{"disambiguationData":[TD([makeQuery(id+"F3.boolean.opBoolean","COPY",FACE,{"derivedFrom":makeQuery(id+"F3.opExtrude","SWEPT_FACE",FACE,{"disambiguationData":[OSD([subQ1])]})})])],"derivedFrom":makeQuery(id+"F3.boolean.opBoolean","COPY",EDGE,{"derivedFrom":makeQuery(id+"F3.opExtrude","CAP_EDGE",EDGE,{"disambiguationData":[OSD([subQ0])],"isStart":false})})});}
            var Q12;
            {var subQ0=sQuery(id+"F2.wireOp",EDGE,"E4.0");var subQ1=makeQuery(id+"F3.boolean.opBoolean","COPY",FACE,{"derivedFrom":makeQuery(id+"F3.opExtrude","SWEPT_FACE",FACE,{"disambiguationData":[OSD([subQ0])]})});var subQ2=sQuery(id+"F2.wireOp",EDGE,"E1.0");Q12=makeQuery(id+"F13.boolean.opBoolean","SPLIT",EDGE,{"disambiguationData":[TD([subQ1])],"derivedFrom":makeQuery(id+"F11.boolean.opBoolean","SPLIT",EDGE,{"disambiguationData":[TD([subQ1])],"derivedFrom":makeQuery(id+"F3.boolean.opBoolean","COPY",EDGE,{"derivedFrom":makeQuery(id+"F3.opExtrude","CAP_EDGE",EDGE,{"disambiguationData":[OSD([subQ2])],"isStart":false})})})});}
            var Q13;
            Q13=makeQuery(id+"F13.boolean.opBoolean","INTERSECT",EDGE,{"derivedFrom":[makeQuery(id+"F3.boolean.opBoolean","COPY",FACE,{"derivedFrom":makeQuery(id+"F3.opExtrude","SWEPT_FACE",FACE,{"disambiguationData":[OSD([sQuery(id+"F2.wireOp",EDGE,"E1.0")])]})}),makeQuery(id+"F13.opExtrude","SWEPT_FACE",FACE,{"disambiguationData":[OSD([sQuery(id+"F12.wireOp",EDGE,"E56.0")])]})]});
            fillet(context, id + "F31", {"entities" : qUnion([Q0, Q1, Q2, Q3, Q4, Q5, Q6, Q7, Q8, Q9, Q10, Q11, Q12, Q13]), "radius" : 0.38 * mm, "tangentPropagation" : true, "allowEdgeOverflow" : false});
        }
        {
            var Q0;
            Q0=makeQuery(id+"F3.boolean.opBoolean","COPY",FACE,{"derivedFrom":makeQuery(id+"F3.opExtrude","SWEPT_FACE",FACE,{"disambiguationData":[OSD([sQuery(id+"F2.wireOp",EDGE,"E3.0")])]})});
            var sketch = newSketch(context, id + "F32", { "sketchPlane" : qUnion([Q0])});
            skLineSegment(sketch, "E113", {"start": v(29.72, 14.73) * mm, "end": v(29.72, 0) * mm});
            skLineSegment(sketch, "E114", {"start": v(63.93, 14.73) * mm, "end": v(63.93, 0) * mm});
            skLineSegment(sketch, "E115", {"start": v(63.93, 0) * mm, "end": v(29.72, 0) * mm});
            skLineSegment(sketch, "E116", {"start": v(29.72, 14.73) * mm, "end": v(63.93, 14.73) * mm});
            skSolve(sketch);
        }
        {
            var Q0;
            Q0=makeQuery(id+"F32.imprint","IMPRINT",FACE,{"disambiguationData":[TD([[makeQuery(id+"F32.imprint","IMPRINT",EDGE,{"derivedFrom":sQuery(id+"F32.wireOp",EDGE,"E113")}),1.0]])]});
            var Q1;
            Q1=makeQuery(id+"F32.imprint","IMPRINT",FACE,{"disambiguationData":[TD([[makeQuery(id+"F32.imprint","IMPRINT",EDGE,{"derivedFrom":sQuery(id+"F32.wireOp",EDGE,"E116")}),-1.0]])]});
            extrude(context, id + "F33", {"entities" : qUnion([Q0, Q1]), "operationType" : NewBodyOperationType.REMOVE, "oppositeDirection" : true, "depth" : 2.03 * mm, "offsetDistance" : 25.4 * mm});
        }
        {
            var Q0;
            Q0=makeQuery(id+"F33.boolean.opBoolean","MERGE",EDGE,{"derivedFrom":[makeQuery(id+"F7.boolean.opBoolean","INTERSECT",EDGE,{"derivedFrom":[makeQuery(id+"F3.boolean.opBoolean","COPY",FACE,{"derivedFrom":makeQuery(id+"F3.opExtrude","SWEPT_FACE",FACE,{"disambiguationData":[OSD([sQuery(id+"F2.wireOp",EDGE,"E3.0")])]})}),makeQuery(id+"F7.opExtrude","SWEPT_FACE",FACE,{"disambiguationData":[OSD([sQuery(id+"F6.wireOp",EDGE,"E17.0")])]})]})],"fromTools":[makeQuery(id+"F33.opExtrude","CAP_EDGE",EDGE,{"disambiguationData":[OSD([sQuery(id+"F32.wireOp",EDGE,"E114")])],"isStart":true})]});
            var Q1;
            Q1=makeQuery(id+"F33.boolean.opBoolean","INTERSECT",EDGE,{"derivedFrom":[makeQuery(id+"F7.boolean.opBoolean","COPY",FACE,{"derivedFrom":makeQuery(id+"F7.opExtrude","SWEPT_FACE",FACE,{"disambiguationData":[OSD([sQuery(id+"F6.wireOp",EDGE,"E18.0")])]})}),makeQuery(id+"F33.opExtrude","CAP_FACE",FACE,{"disambiguationData":[OSD([sQuery(id+"F32.wireOp",EDGE,"E113"),sQuery(id+"F32.wireOp",EDGE,"E114"),sQuery(id+"F32.wireOp",EDGE,"E115"),sQuery(id+"F32.wireOp",EDGE,"E116")])],"isStart":false})]});
            fillet(context, id + "F34", {"entities" : qUnion([Q0, Q1]), "radius" : 0.38 * mm, "tangentPropagation" : true, "allowEdgeOverflow" : false});
        }
        {
            var Q0;
            Q0=makeQuery(id+"F33.boolean.opBoolean","COPY",EDGE,{"derivedFrom":makeQuery(id+"F33.opExtrude","CAP_EDGE",EDGE,{"disambiguationData":[OSD([sQuery(id+"F32.wireOp",EDGE,"E114")])],"isStart":false})});
            var Q1;
            Q1=makeQuery(id+"F33.boolean.opBoolean","COPY",EDGE,{"derivedFrom":makeQuery(id+"F33.opExtrude","CAP_EDGE",EDGE,{"disambiguationData":[OSD([sQuery(id+"F32.wireOp",EDGE,"E113")])],"isStart":false})});
            fillet(context, id + "F35", {"entities" : qUnion([Q0, Q1]), "radius" : 0.38 * mm, "tangentPropagation" : true, "allowEdgeOverflow" : false});
        }
    });
